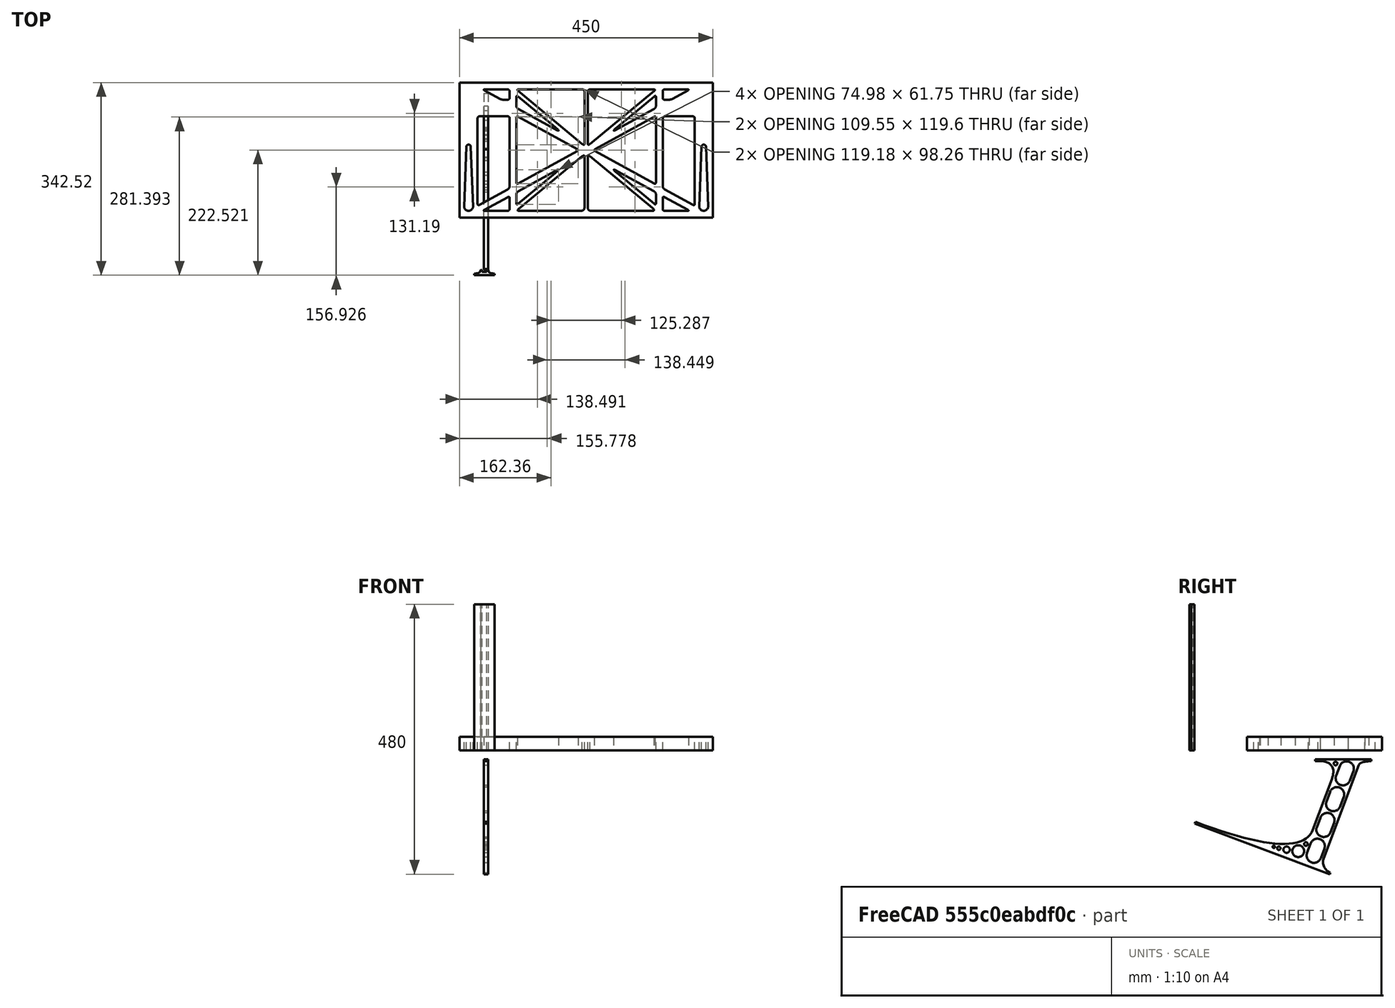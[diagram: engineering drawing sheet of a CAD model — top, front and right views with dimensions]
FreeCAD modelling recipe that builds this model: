
FCSTD DOCUMENT  (FreeCAD 0.19R0.19.2)
Label: laptopStand157FCStd
License: All rights reserved
LicenseURL: http://en.wikipedia.org/wiki/All_rights_reserved
objects: Sketcher::SketchObject×4, Part::Extrusion×3
note: 7 computed .brp shape members not serialized (recipe doc carries the construction recipe); baked Part::Feature solids carry a one-line shape summary decoded from their .brp

FEATURE [Sketcher::SketchObject] Sketch
  FullyConstrained = false
  sketch-geometry (349):
    g0: LineSegment StartX=-10.9272 StartY=-82.7794 StartZ=0 EndX=46.0728 EndY=-51.4823 EndZ=0
    g1: LineSegment StartX=-10.9272 StartY=76.4095 StartZ=0 EndX=-10.9272 EndY=-82.7794 EndZ=0
    g2: LineSegment StartX=46.0728 StartY=76.4095 StartZ=0 EndX=46.0728 EndY=-51.4823 EndZ=0
    g3: LineSegment StartX=-42.9272 StartY=136.221 StartZ=0 EndX=-42.9272 EndY=-103.779 EndZ=0
    g4: LineSegment StartX=407.073 StartY=136.221 StartZ=0 EndX=407.073 EndY=-103.779 EndZ=0
    g5: ArcOfCircle CenterX=-26.9272 CenterY=-83.7794 CenterZ=0 NormalX=0 NormalY=0 NormalZ=1 AngleXU=0 Radius=8 StartAngle=3.14159 EndAngle=6.28319
    g6: ArcOfCircle CenterX=391.073 CenterY=22.1087 CenterZ=0 NormalX=0 NormalY=0 NormalZ=1 AngleXU=0 Radius=8 StartAngle=-4.4e-15 EndAngle=3.14159
    g7: LineSegment StartX=399.073 StartY=22.1087 StartZ=0 EndX=399.073 EndY=-83.7794 EndZ=0
    g8: LineSegment StartX=383.073 StartY=22.1087 StartZ=0 EndX=383.073 EndY=-83.7794 EndZ=0
    g9: ArcOfCircle CenterX=391.073 CenterY=-83.7794 CenterZ=0 NormalX=0 NormalY=0 NormalZ=1 AngleXU=0 Radius=8 StartAngle=3.14159 EndAngle=6.28319
    g10: Circle CenterX=175.022 CenterY=27.0628 CenterZ=0 NormalX=0 NormalY=0 NormalZ=1 AngleXU=0 Radius=1
    g11: Circle CenterX=179.022 CenterY=24.8665 CenterZ=0 NormalX=0 NormalY=0 NormalZ=1 AngleXU=0 Radius=1
    g12: Circle CenterX=179.022 CenterY=27.0628 CenterZ=0 NormalX=0 NormalY=0 NormalZ=1 AngleXU=0 Radius=1
    g13: BSplineCurve PolesCount=3 KnotsCount=2 Degree=2 IsPeriodic=0
    g14: GeomPoint X=175.022 Y=27.0628 Z=0
    g15: GeomPoint X=179.022 Y=27.0628 Z=0
    g16: Circle CenterX=189.124 CenterY=27.0628 CenterZ=0 NormalX=0 NormalY=0 NormalZ=1 AngleXU=0 Radius=1
    g17: Circle CenterX=185.124 CenterY=24.8665 CenterZ=0 NormalX=0 NormalY=0 NormalZ=1 AngleXU=0 Radius=1
    g18: Circle CenterX=185.124 CenterY=27.0628 CenterZ=0 NormalX=0 NormalY=0 NormalZ=1 AngleXU=0 Radius=1
    g19: BSplineCurve PolesCount=3 KnotsCount=2 Degree=2 IsPeriodic=0
    g20: GeomPoint X=189.124 Y=27.0628 Z=0
    g21: GeomPoint X=185.124 Y=27.0628 Z=0
    g22: Circle CenterX=175.022 CenterY=5.37834 CenterZ=0 NormalX=0 NormalY=0 NormalZ=1 AngleXU=0 Radius=1
    g23: Circle CenterX=179.022 CenterY=7.57463 CenterZ=0 NormalX=0 NormalY=0 NormalZ=1 AngleXU=0 Radius=1
    g24: Circle CenterX=179.022 CenterY=5.34704 CenterZ=0 NormalX=0 NormalY=0 NormalZ=1 AngleXU=0 Radius=1
    g25: BSplineCurve PolesCount=3 KnotsCount=2 Degree=2 IsPeriodic=0
    g26: GeomPoint X=175.022 Y=5.37834 Z=0
    g27: GeomPoint X=179.022 Y=5.34704 Z=0
    g28: Circle CenterX=189.124 CenterY=5.37834 CenterZ=0 NormalX=0 NormalY=0 NormalZ=1 AngleXU=0 Radius=1
    g29: Circle CenterX=185.124 CenterY=7.57463 CenterZ=0 NormalX=0 NormalY=0 NormalZ=1 AngleXU=0 Radius=1
    g30: Circle CenterX=185.124 CenterY=5.34704 CenterZ=0 NormalX=0 NormalY=0 NormalZ=1 AngleXU=0 Radius=1
    g31: BSplineCurve PolesCount=3 KnotsCount=2 Degree=2 IsPeriodic=0
    g32: GeomPoint X=189.124 Y=5.37834 Z=0
    g33: GeomPoint X=185.124 Y=5.34704 Z=0
    g34: Circle CenterX=165.871 CenterY=18.1458 CenterZ=0 NormalX=0 NormalY=0 NormalZ=1 AngleXU=0 Radius=1
    g35: Circle CenterX=169.377 CenterY=16.2206 CenterZ=0 NormalX=0 NormalY=0 NormalZ=1 AngleXU=0 Radius=1
    g36: Circle CenterX=165.871 CenterY=14.2954 CenterZ=0 NormalX=0 NormalY=0 NormalZ=1 AngleXU=0 Radius=1
    g37: BSplineCurve PolesCount=3 KnotsCount=2 Degree=2 IsPeriodic=0
    g38: GeomPoint X=165.871 Y=18.1458 Z=0
    g39: GeomPoint X=165.871 Y=14.2954 Z=0
    g40: Circle CenterX=198.275 CenterY=18.1458 CenterZ=0 NormalX=0 NormalY=0 NormalZ=1 AngleXU=0 Radius=1
    g41: Circle CenterX=194.768 CenterY=16.2206 CenterZ=0 NormalX=0 NormalY=0 NormalZ=1 AngleXU=0 Radius=1
    g42: Circle CenterX=198.275 CenterY=14.2954 CenterZ=0 NormalX=0 NormalY=0 NormalZ=1 AngleXU=0 Radius=1
    g43: BSplineCurve PolesCount=3 KnotsCount=2 Degree=2 IsPeriodic=0
    g44: GeomPoint X=198.275 Y=18.1458 Z=0
    g45: GeomPoint X=198.275 Y=14.2954 Z=0
    g46: LineSegment StartX=407.073 StartY=-103.779 StartZ=0 EndX=-42.9272 EndY=-103.779 EndZ=0
    g47: LineSegment StartX=407.073 StartY=136.221 StartZ=0 EndX=-42.9272 EndY=136.221 EndZ=0
    g48: LineSegment StartX=46.0728 StartY=76.4095 StartZ=0 EndX=-10.9272 EndY=76.4095 EndZ=0
    g49: Circle CenterX=125.607 CenterY=54.1951 CenterZ=0 NormalX=0 NormalY=0 NormalZ=1 AngleXU=0 Radius=1
    g50: Circle CenterX=139.632 CenterY=46.4944 CenterZ=0 NormalX=0 NormalY=0 NormalZ=1 AngleXU=0 Radius=1
    g51: Circle CenterX=127.326 CenterY=56.7187 CenterZ=0 NormalX=0 NormalY=0 NormalZ=1 AngleXU=0 Radius=1
    g52: BSplineCurve PolesCount=3 KnotsCount=2 Degree=2 IsPeriodic=0
    g53: GeomPoint X=125.607 Y=54.1951 Z=0
    g54: GeomPoint X=127.326 Y=56.7187 Z=0
    g55: Circle CenterX=236.821 CenterY=56.7187 CenterZ=0 NormalX=0 NormalY=0 NormalZ=1 AngleXU=0 Radius=1
    g56: Circle CenterX=224.513 CenterY=46.4944 CenterZ=0 NormalX=0 NormalY=0 NormalZ=1 AngleXU=0 Radius=1
    g57: Circle CenterX=238.538 CenterY=54.1951 CenterZ=0 NormalX=0 NormalY=0 NormalZ=1 AngleXU=0 Radius=1
    g58: BSplineCurve PolesCount=3 KnotsCount=2 Degree=2 IsPeriodic=0
    g59: GeomPoint X=236.821 Y=56.7187 Z=0
    g60: GeomPoint X=238.538 Y=54.1951 Z=0
    g61: Circle CenterX=238.538 CenterY=-21.7539 CenterZ=0 NormalX=0 NormalY=0 NormalZ=1 AngleXU=0 Radius=1
    g62: Circle CenterX=224.513 CenterY=-14.0532 CenterZ=0 NormalX=0 NormalY=0 NormalZ=1 AngleXU=0 Radius=1
    g63: Circle CenterX=236.821 CenterY=-24.2775 CenterZ=0 NormalX=0 NormalY=0 NormalZ=1 AngleXU=0 Radius=1
    g64: BSplineCurve PolesCount=3 KnotsCount=2 Degree=2 IsPeriodic=0
    g65: GeomPoint X=238.538 Y=-21.7539 Z=0
    g66: GeomPoint X=236.821 Y=-24.2775 Z=0
    g67: Circle CenterX=125.607 CenterY=-21.7539 CenterZ=0 NormalX=0 NormalY=0 NormalZ=1 AngleXU=0 Radius=1
    g68: Circle CenterX=139.632 CenterY=-14.0532 CenterZ=0 NormalX=0 NormalY=0 NormalZ=1 AngleXU=0 Radius=1
    g69: Circle CenterX=127.325 CenterY=-24.2775 CenterZ=0 NormalX=0 NormalY=0 NormalZ=1 AngleXU=0 Radius=1
    g70: BSplineCurve PolesCount=3 KnotsCount=2 Degree=2 IsPeriodic=0
    g71: GeomPoint X=125.607 Y=-21.7539 Z=0
    g72: GeomPoint X=127.325 Y=-24.2775 Z=0
    g73: Circle CenterX=302.996 CenterY=111.695 CenterZ=0 NormalX=0 NormalY=0 NormalZ=1 AngleXU=0 Radius=1
    g74: Circle CenterX=306.073 CenterY=114.251 CenterZ=0 NormalX=0 NormalY=0 NormalZ=1 AngleXU=0 Radius=1
    g75: Circle CenterX=306.073 CenterY=110.251 CenterZ=0 NormalX=0 NormalY=0 NormalZ=1 AngleXU=0 Radius=1
    g76: BSplineCurve PolesCount=3 KnotsCount=2 Degree=2 IsPeriodic=0
    g77: GeomPoint X=302.996 Y=111.695 Z=0
    g78: GeomPoint X=306.073 Y=110.251 Z=0
    g79: Circle CenterX=306.073 CenterY=95.2763 CenterZ=0 NormalX=0 NormalY=0 NormalZ=1 AngleXU=0 Radius=1
    g80: Circle CenterX=306.073 CenterY=91.2763 CenterZ=0 NormalX=0 NormalY=0 NormalZ=1 AngleXU=0 Radius=1
    g81: Circle CenterX=302.567 CenterY=89.3511 CenterZ=0 NormalX=0 NormalY=0 NormalZ=1 AngleXU=0 Radius=1
    g82: BSplineCurve PolesCount=3 KnotsCount=2 Degree=2 IsPeriodic=0
    g83: GeomPoint X=306.073 Y=95.2763 Z=0
    g84: GeomPoint X=302.567 Y=89.3511 Z=0
    g85: LineSegment StartX=306.073 StartY=110.251 StartZ=0 EndX=306.073 EndY=95.2763 EndZ=0
    g86: LineSegment StartX=302.996 StartY=111.695 StartZ=0 EndX=236.821 EndY=56.7187 EndZ=0
    g87: LineSegment StartX=238.538 StartY=54.1951 StartZ=0 EndX=302.567 EndY=89.3511 EndZ=0
    g88: Circle CenterX=61.1496 CenterY=111.695 CenterZ=0 NormalX=0 NormalY=0 NormalZ=1 AngleXU=0 Radius=1
    g89: Circle CenterX=58.0728 CenterY=114.251 CenterZ=0 NormalX=0 NormalY=0 NormalZ=1 AngleXU=0 Radius=1
    g90: Circle CenterX=58.0728 CenterY=110.251 CenterZ=0 NormalX=0 NormalY=0 NormalZ=1 AngleXU=0 Radius=1
    g91: BSplineCurve PolesCount=3 KnotsCount=2 Degree=2 IsPeriodic=0
    g92: GeomPoint X=61.1496 Y=111.695 Z=0
    g93: GeomPoint X=58.0728 Y=110.251 Z=0
    g94: Circle CenterX=61.5791 CenterY=89.3511 CenterZ=0 NormalX=0 NormalY=0 NormalZ=1 AngleXU=0 Radius=1
    g95: Circle CenterX=58.0728 CenterY=91.2763 CenterZ=0 NormalX=0 NormalY=0 NormalZ=1 AngleXU=0 Radius=1
    g96: Circle CenterX=58.0728 CenterY=95.2763 CenterZ=0 NormalX=0 NormalY=0 NormalZ=1 AngleXU=0 Radius=1
    g97: BSplineCurve PolesCount=3 KnotsCount=2 Degree=2 IsPeriodic=0
    g98: GeomPoint X=61.5791 Y=89.3511 Z=0
    g99: GeomPoint X=58.0728 Y=95.2763 Z=0
    g100: LineSegment StartX=58.0728 StartY=110.251 StartZ=0 EndX=58.0728 EndY=95.2763 EndZ=0
    g101: LineSegment StartX=61.1496 StartY=111.695 StartZ=0 EndX=127.326 EndY=56.7187 EndZ=0
    g102: LineSegment StartX=125.607 StartY=54.1951 StartZ=0 EndX=61.5791 EndY=89.3511 EndZ=0
    g103: Circle CenterX=61.5791 CenterY=-56.9099 CenterZ=0 NormalX=0 NormalY=0 NormalZ=1 AngleXU=0 Radius=1
    g104: Circle CenterX=58.0728 CenterY=-58.8351 CenterZ=0 NormalX=0 NormalY=0 NormalZ=1 AngleXU=0 Radius=1
    g105: Circle CenterX=58.0728 CenterY=-62.8351 CenterZ=0 NormalX=0 NormalY=0 NormalZ=1 AngleXU=0 Radius=1
    g106: BSplineCurve PolesCount=3 KnotsCount=2 Degree=2 IsPeriodic=0
    g107: GeomPoint X=61.5791 Y=-56.9099 Z=0
    g108: GeomPoint X=58.0728 Y=-62.8351 Z=0
    g109: Circle CenterX=58.0728 CenterY=-77.8102 CenterZ=0 NormalX=0 NormalY=0 NormalZ=1 AngleXU=0 Radius=1
    g110: Circle CenterX=58.0728 CenterY=-81.8102 CenterZ=0 NormalX=0 NormalY=0 NormalZ=1 AngleXU=0 Radius=1
    g111: Circle CenterX=61.1496 CenterY=-79.2541 CenterZ=0 NormalX=0 NormalY=0 NormalZ=1 AngleXU=0 Radius=1
    g112: BSplineCurve PolesCount=3 KnotsCount=2 Degree=2 IsPeriodic=0
    g113: GeomPoint X=58.0728 Y=-77.8102 Z=0
    g114: GeomPoint X=61.1496 Y=-79.2541 Z=0
    g115: LineSegment StartX=58.0728 StartY=-62.8351 StartZ=0 EndX=58.0728 EndY=-77.8102 EndZ=0
    g116: LineSegment StartX=61.1496 StartY=-79.2541 StartZ=0 EndX=127.325 EndY=-24.2775 EndZ=0
    g117: LineSegment StartX=125.607 StartY=-21.7539 StartZ=0 EndX=61.5791 EndY=-56.9099 EndZ=0
    g118: Circle CenterX=302.567 CenterY=-56.9099 CenterZ=0 NormalX=0 NormalY=0 NormalZ=1 AngleXU=0 Radius=1
    g119: Circle CenterX=306.073 CenterY=-58.8351 CenterZ=0 NormalX=0 NormalY=0 NormalZ=1 AngleXU=0 Radius=1
    g120: Circle CenterX=306.073 CenterY=-62.8351 CenterZ=0 NormalX=0 NormalY=0 NormalZ=1 AngleXU=0 Radius=1
    g121: BSplineCurve PolesCount=3 KnotsCount=2 Degree=2 IsPeriodic=0
    g122: GeomPoint X=302.567 Y=-56.9099 Z=0
    g123: GeomPoint X=306.073 Y=-62.8351 Z=0
    g124: Circle CenterX=302.996 CenterY=-79.2541 CenterZ=0 NormalX=0 NormalY=0 NormalZ=1 AngleXU=0 Radius=1
    g125: Circle CenterX=306.073 CenterY=-81.8102 CenterZ=0 NormalX=0 NormalY=0 NormalZ=1 AngleXU=0 Radius=1
    g126: Circle CenterX=306.073 CenterY=-77.8102 CenterZ=0 NormalX=0 NormalY=0 NormalZ=1 AngleXU=0 Radius=1
    g127: BSplineCurve PolesCount=3 KnotsCount=2 Degree=2 IsPeriodic=0
    g128: GeomPoint X=302.996 Y=-79.2541 Z=0
    g129: GeomPoint X=306.073 Y=-77.8102 Z=0
    g130: LineSegment StartX=306.073 StartY=-62.8351 StartZ=0 EndX=306.073 EndY=-77.8102 EndZ=0
    g131: LineSegment StartX=302.996 StartY=-79.2541 StartZ=0 EndX=236.821 EndY=-24.2775 EndZ=0
    g132: LineSegment StartX=238.538 StartY=-21.7539 StartZ=0 EndX=302.567 EndY=-56.9099 EndZ=0
    g133: Circle CenterX=61.6457 CenterY=-88.8112 CenterZ=0 NormalX=0 NormalY=0 NormalZ=1 AngleXU=0 Radius=1
    g134: Circle CenterX=58.0728 CenterY=-91.7794 CenterZ=0 NormalX=0 NormalY=0 NormalZ=1 AngleXU=0 Radius=1
    g135: Circle CenterX=63.9135 CenterY=-91.7794 CenterZ=0 NormalX=0 NormalY=0 NormalZ=1 AngleXU=0 Radius=1
    g136: BSplineCurve PolesCount=3 KnotsCount=2 Degree=2 IsPeriodic=0
    g137: GeomPoint X=61.6457 Y=-88.8112 Z=0
    g138: GeomPoint X=63.9135 Y=-91.7794 Z=0
    g139: Circle CenterX=179.022 CenterY=-85.8163 CenterZ=0 NormalX=0 NormalY=0 NormalZ=1 AngleXU=0 Radius=1
    g140: Circle CenterX=179.022 CenterY=-91.7794 CenterZ=0 NormalX=0 NormalY=0 NormalZ=1 AngleXU=0 Radius=1
    g141: Circle CenterX=171.895 CenterY=-91.7794 CenterZ=0 NormalX=0 NormalY=0 NormalZ=1 AngleXU=0 Radius=1
    g142: BSplineCurve PolesCount=3 KnotsCount=2 Degree=2 IsPeriodic=0
    g143: GeomPoint X=179.022 Y=-85.8163 Z=0
    g144: GeomPoint X=171.895 Y=-91.7794 Z=0
    g145: Circle CenterX=185.124 CenterY=-86.2028 CenterZ=0 NormalX=0 NormalY=0 NormalZ=1 AngleXU=0 Radius=1
    g146: Circle CenterX=185.124 CenterY=-91.7794 CenterZ=0 NormalX=0 NormalY=0 NormalZ=1 AngleXU=0 Radius=1
    g147: Circle CenterX=191.747 CenterY=-91.7794 CenterZ=0 NormalX=0 NormalY=0 NormalZ=1 AngleXU=0 Radius=1
    g148: BSplineCurve PolesCount=3 KnotsCount=2 Degree=2 IsPeriodic=0
    g149: GeomPoint X=185.124 Y=-86.2028 Z=0
    g150: GeomPoint X=191.747 Y=-91.7794 Z=0
    g151: Circle CenterX=299.888 CenterY=-86.6413 CenterZ=0 NormalX=0 NormalY=0 NormalZ=1 AngleXU=0 Radius=1
    g152: Circle CenterX=306.073 CenterY=-91.7794 CenterZ=0 NormalX=0 NormalY=0 NormalZ=1 AngleXU=0 Radius=1
    g153: Circle CenterX=298.776 CenterY=-91.7794 CenterZ=0 NormalX=0 NormalY=0 NormalZ=1 AngleXU=0 Radius=1
    g154: BSplineCurve PolesCount=3 KnotsCount=2 Degree=2 IsPeriodic=0
    g155: GeomPoint X=299.888 Y=-86.6413 Z=0
    g156: GeomPoint X=298.776 Y=-91.7794 Z=0
    g157: LineSegment StartX=189.124 StartY=5.37834 StartZ=0 EndX=299.888 EndY=-86.6413 EndZ=0
    g158: LineSegment StartX=298.776 StartY=-91.7794 StartZ=0 EndX=191.747 EndY=-91.7794 EndZ=0
    g159: LineSegment StartX=185.124 StartY=-86.2028 StartZ=0 EndX=185.124 EndY=5.34704 EndZ=0
    g160: LineSegment StartX=179.022 StartY=5.34704 StartZ=0 EndX=179.022 EndY=-85.8163 EndZ=0
    g161: LineSegment StartX=171.895 StartY=-91.7794 StartZ=0 EndX=63.9135 EndY=-91.7794 EndZ=0
    g162: LineSegment StartX=61.6457 StartY=-88.8112 StartZ=0 EndX=175.022 EndY=5.37834 EndZ=0
    g163: Circle CenterX=302.073 CenterY=124.221 CenterZ=0 NormalX=0 NormalY=0 NormalZ=1 AngleXU=0 Radius=1
    g164: Circle CenterX=306.073 CenterY=124.221 CenterZ=0 NormalX=0 NormalY=0 NormalZ=1 AngleXU=0 Radius=1
    g165: Circle CenterX=302.996 CenterY=121.665 CenterZ=0 NormalX=0 NormalY=0 NormalZ=1 AngleXU=0 Radius=1
    g166: BSplineCurve PolesCount=3 KnotsCount=2 Degree=2 IsPeriodic=0
    g167: GeomPoint X=302.073 Y=124.221 Z=0
    g168: GeomPoint X=302.996 Y=121.665 Z=0
    g169: Circle CenterX=189.124 CenterY=124.221 CenterZ=0 NormalX=0 NormalY=0 NormalZ=1 AngleXU=0 Radius=1
    g170: Circle CenterX=185.124 CenterY=124.221 CenterZ=0 NormalX=0 NormalY=0 NormalZ=1 AngleXU=0 Radius=1
    g171: Circle CenterX=185.124 CenterY=120.221 CenterZ=0 NormalX=0 NormalY=0 NormalZ=1 AngleXU=0 Radius=1
    g172: BSplineCurve PolesCount=3 KnotsCount=2 Degree=2 IsPeriodic=0
    g173: GeomPoint X=189.124 Y=124.221 Z=0
    g174: GeomPoint X=185.124 Y=120.221 Z=0
    g175: Circle CenterX=175.022 CenterY=124.221 CenterZ=0 NormalX=0 NormalY=0 NormalZ=1 AngleXU=0 Radius=1
    g176: Circle CenterX=179.022 CenterY=124.221 CenterZ=0 NormalX=0 NormalY=0 NormalZ=1 AngleXU=0 Radius=1
    g177: Circle CenterX=179.022 CenterY=120.221 CenterZ=0 NormalX=0 NormalY=0 NormalZ=1 AngleXU=0 Radius=1
    g178: BSplineCurve PolesCount=3 KnotsCount=2 Degree=2 IsPeriodic=0
    g179: GeomPoint X=175.022 Y=124.221 Z=0
    g180: GeomPoint X=179.022 Y=120.221 Z=0
    g181: Circle CenterX=62.0728 CenterY=124.221 CenterZ=0 NormalX=0 NormalY=0 NormalZ=1 AngleXU=0 Radius=1
    g182: Circle CenterX=58.0728 CenterY=124.221 CenterZ=0 NormalX=0 NormalY=0 NormalZ=1 AngleXU=0 Radius=1
    g183: Circle CenterX=61.1496 CenterY=121.665 CenterZ=0 NormalX=0 NormalY=0 NormalZ=1 AngleXU=0 Radius=1
    g184: BSplineCurve PolesCount=3 KnotsCount=2 Degree=2 IsPeriodic=0
    g185: GeomPoint X=62.0728 Y=124.221 Z=0
    g186: GeomPoint X=61.1496 Y=121.665 Z=0
    g187: LineSegment StartX=62.0728 StartY=124.221 StartZ=0 EndX=175.022 EndY=124.221 EndZ=0
    g188: LineSegment StartX=179.022 StartY=120.221 StartZ=0 EndX=179.022 EndY=27.0628 EndZ=0
    g189: LineSegment StartX=185.124 StartY=27.0628 StartZ=0 EndX=185.124 EndY=120.221 EndZ=0
    g190: LineSegment StartX=189.124 StartY=124.221 StartZ=0 EndX=302.073 EndY=124.221 EndZ=0
    g191: LineSegment StartX=302.996 StartY=121.665 StartZ=0 EndX=189.124 EndY=27.0628 EndZ=0
    g192: LineSegment StartX=175.022 StartY=27.0628 StartZ=0 EndX=61.1496 EndY=121.665 EndZ=0
    g193: Circle CenterX=61.5791 CenterY=75.4095 CenterZ=0 NormalX=0 NormalY=0 NormalZ=1 AngleXU=0 Radius=1
    g194: Circle CenterX=58.0728 CenterY=77.3346 CenterZ=0 NormalX=0 NormalY=0 NormalZ=1 AngleXU=0 Radius=1
    g195: Circle CenterX=58.0728 CenterY=73.3346 CenterZ=0 NormalX=0 NormalY=0 NormalZ=1 AngleXU=0 Radius=1
    g196: BSplineCurve PolesCount=3 KnotsCount=2 Degree=2 IsPeriodic=0
    g197: GeomPoint X=61.5791 Y=75.4095 Z=0
    g198: GeomPoint X=58.0728 Y=73.3346 Z=0
    g199: Circle CenterX=58.0728 CenterY=-40.8935 CenterZ=0 NormalX=0 NormalY=0 NormalZ=1 AngleXU=0 Radius=1
    g200: Circle CenterX=58.0728 CenterY=-44.8935 CenterZ=0 NormalX=0 NormalY=0 NormalZ=1 AngleXU=0 Radius=1
    g201: Circle CenterX=61.5791 CenterY=-42.9683 CenterZ=0 NormalX=0 NormalY=0 NormalZ=1 AngleXU=0 Radius=1
    g202: BSplineCurve PolesCount=3 KnotsCount=2 Degree=2 IsPeriodic=0
    g203: GeomPoint X=58.0728 Y=-40.8935 Z=0
    g204: GeomPoint X=61.5791 Y=-42.9683 Z=0
    g205: LineSegment StartX=61.5791 StartY=-42.9683 StartZ=0 EndX=165.871 EndY=14.2954 EndZ=0
    g206: LineSegment StartX=165.871 StartY=18.1458 StartZ=0 EndX=61.5791 EndY=75.4095 EndZ=0
    g207: LineSegment StartX=58.0728 StartY=73.3346 StartZ=0 EndX=58.0728 EndY=-40.8935 EndZ=0
    g208: Circle CenterX=302.567 CenterY=-42.9683 CenterZ=0 NormalX=0 NormalY=0 NormalZ=1 AngleXU=0 Radius=1
    g209: Circle CenterX=306.073 CenterY=-44.8935 CenterZ=0 NormalX=0 NormalY=0 NormalZ=1 AngleXU=0 Radius=1
    g210: Circle CenterX=306.073 CenterY=-40.8935 CenterZ=0 NormalX=0 NormalY=0 NormalZ=1 AngleXU=0 Radius=1
    g211: BSplineCurve PolesCount=3 KnotsCount=2 Degree=2 IsPeriodic=0
    g212: GeomPoint X=302.567 Y=-42.9683 Z=0
    g213: GeomPoint X=306.073 Y=-40.8935 Z=0
    g214: Circle CenterX=306.073 CenterY=73.3346 CenterZ=0 NormalX=0 NormalY=0 NormalZ=1 AngleXU=0 Radius=1
    g215: Circle CenterX=306.073 CenterY=77.3346 CenterZ=0 NormalX=0 NormalY=0 NormalZ=1 AngleXU=0 Radius=1
    g216: Circle CenterX=302.567 CenterY=75.4095 CenterZ=0 NormalX=0 NormalY=0 NormalZ=1 AngleXU=0 Radius=1
    g217: BSplineCurve PolesCount=3 KnotsCount=2 Degree=2 IsPeriodic=0
    g218: GeomPoint X=306.073 Y=73.3346 Z=0
    g219: GeomPoint X=302.567 Y=75.4095 Z=0
    g220: LineSegment StartX=302.567 StartY=-42.9683 StartZ=0 EndX=198.275 EndY=14.2954 EndZ=0
    g221: LineSegment StartX=198.275 StartY=18.1458 StartZ=0 EndX=302.567 EndY=75.4095 EndZ=0
    g222: LineSegment StartX=306.073 StartY=73.3346 StartZ=0 EndX=306.073 EndY=-40.8935 EndZ=0
    g223: LineSegment StartX=322.073 StartY=105.865 StartZ=0 EndX=328.643 EndY=105.865 EndZ=0
    g224: LineSegment StartX=318.073 StartY=120.221 StartZ=0 EndX=318.073 EndY=109.865 EndZ=0
    g225: LineSegment StartX=336.157 StartY=107.779 StartZ=0 EndX=362.567 EndY=122.294 EndZ=0
    g226: Circle CenterX=362.073 CenterY=124.221 CenterZ=0 NormalX=0 NormalY=0 NormalZ=1 AngleXU=0 Radius=1
    g227: Circle CenterX=366.073 CenterY=124.221 CenterZ=0 NormalX=0 NormalY=0 NormalZ=1 AngleXU=0 Radius=1
    g228: Circle CenterX=362.567 CenterY=122.294 CenterZ=0 NormalX=0 NormalY=0 NormalZ=1 AngleXU=0 Radius=1
    g229: BSplineCurve PolesCount=3 KnotsCount=2 Degree=2 IsPeriodic=0
    g230: GeomPoint X=362.073 Y=124.221 Z=0
    g231: GeomPoint X=362.567 Y=122.294 Z=0
    g232: Circle CenterX=322.073 CenterY=124.221 CenterZ=0 NormalX=0 NormalY=0 NormalZ=1 AngleXU=0 Radius=1
    g233: Circle CenterX=318.073 CenterY=124.221 CenterZ=0 NormalX=0 NormalY=0 NormalZ=1 AngleXU=0 Radius=1
    g234: Circle CenterX=318.073 CenterY=120.221 CenterZ=0 NormalX=0 NormalY=0 NormalZ=1 AngleXU=0 Radius=1
    g235: BSplineCurve PolesCount=3 KnotsCount=2 Degree=2 IsPeriodic=0
    g236: GeomPoint X=322.073 Y=124.221 Z=0
    g237: GeomPoint X=318.073 Y=120.221 Z=0
    g238: Circle CenterX=322.073 CenterY=105.865 CenterZ=0 NormalX=0 NormalY=0 NormalZ=1 AngleXU=0 Radius=1
    g239: Circle CenterX=318.073 CenterY=105.865 CenterZ=0 NormalX=0 NormalY=0 NormalZ=1 AngleXU=0 Radius=1
    g240: Circle CenterX=318.073 CenterY=109.865 CenterZ=0 NormalX=0 NormalY=0 NormalZ=1 AngleXU=0 Radius=1
    g241: BSplineCurve PolesCount=3 KnotsCount=2 Degree=2 IsPeriodic=0
    g242: GeomPoint X=322.073 Y=105.865 Z=0
    g243: GeomPoint X=318.073 Y=109.865 Z=0
    g244: Circle CenterX=336.157 CenterY=107.779 CenterZ=0 NormalX=0 NormalY=0 NormalZ=1 AngleXU=0 Radius=1
    g245: Circle CenterX=332.651 CenterY=105.853 CenterZ=0 NormalX=0 NormalY=0 NormalZ=1 AngleXU=0 Radius=1
    g246: Circle CenterX=328.643 CenterY=105.865 CenterZ=0 NormalX=0 NormalY=0 NormalZ=1 AngleXU=0 Radius=1
    g247: BSplineCurve PolesCount=3 KnotsCount=2 Degree=2 IsPeriodic=0
    g248: GeomPoint X=336.157 Y=107.779 Z=0
    g249: GeomPoint X=328.643 Y=105.865 Z=0
    g250: LineSegment StartX=322.073 StartY=124.221 StartZ=0 EndX=362.073 EndY=124.221 EndZ=0
    g251: Circle CenterX=371.567 CenterY=-80.8644 CenterZ=0 NormalX=0 NormalY=0 NormalZ=1 AngleXU=0 Radius=1
    g252: Circle CenterX=375.073 CenterY=-82.7896 CenterZ=0 NormalX=0 NormalY=0 NormalZ=1 AngleXU=0 Radius=1
    g253: Circle CenterX=375.073 CenterY=-78.7896 CenterZ=0 NormalX=0 NormalY=0 NormalZ=1 AngleXU=0 Radius=1
    g254: BSplineCurve PolesCount=3 KnotsCount=2 Degree=2 IsPeriodic=0
    g255: GeomPoint X=371.567 Y=-80.8644 Z=0
    g256: GeomPoint X=375.073 Y=-78.7896 Z=0
    g257: Circle CenterX=321.579 CenterY=-53.4075 CenterZ=0 NormalX=0 NormalY=0 NormalZ=1 AngleXU=0 Radius=1
    g258: Circle CenterX=318.073 CenterY=-51.4823 CenterZ=0 NormalX=0 NormalY=0 NormalZ=1 AngleXU=0 Radius=1
    g259: Circle CenterX=318.073 CenterY=-47.4805 CenterZ=0 NormalX=0 NormalY=0 NormalZ=1 AngleXU=0 Radius=1
    g260: BSplineCurve PolesCount=3 KnotsCount=2 Degree=2 IsPeriodic=0
    g261: GeomPoint X=321.579 Y=-53.4075 Z=0
    g262: GeomPoint X=318.073 Y=-47.4805 Z=0
    g263: LineSegment StartX=371.567 StartY=-80.8644 StartZ=0 EndX=321.579 EndY=-53.4075 EndZ=0
    g264: Circle CenterX=321.579 CenterY=-67.3492 CenterZ=0 NormalX=0 NormalY=0 NormalZ=1 AngleXU=0 Radius=1
    g265: Circle CenterX=318.073 CenterY=-65.424 CenterZ=0 NormalX=0 NormalY=0 NormalZ=1 AngleXU=0 Radius=1
    g266: Circle CenterX=318.073 CenterY=-69.424 CenterZ=0 NormalX=0 NormalY=0 NormalZ=1 AngleXU=0 Radius=1
    g267: BSplineCurve PolesCount=3 KnotsCount=2 Degree=2 IsPeriodic=0
    g268: GeomPoint X=321.579 Y=-67.3492 Z=0
    g269: GeomPoint X=318.073 Y=-69.424 Z=0
    g270: Circle CenterX=362.567 CenterY=-89.8542 CenterZ=0 NormalX=0 NormalY=0 NormalZ=1 AngleXU=0 Radius=1
    g271: Circle CenterX=366.073 CenterY=-91.7794 CenterZ=0 NormalX=0 NormalY=0 NormalZ=1 AngleXU=0 Radius=1
    g272: Circle CenterX=362.073 CenterY=-91.7794 CenterZ=0 NormalX=0 NormalY=0 NormalZ=1 AngleXU=0 Radius=1
    g273: BSplineCurve PolesCount=3 KnotsCount=2 Degree=2 IsPeriodic=0
    g274: GeomPoint X=362.567 Y=-89.8542 Z=0
    g275: GeomPoint X=362.073 Y=-91.7794 Z=0
    g276: Circle CenterX=322.073 CenterY=-91.7794 CenterZ=0 NormalX=0 NormalY=0 NormalZ=1 AngleXU=0 Radius=1
    g277: Circle CenterX=318.073 CenterY=-91.7794 CenterZ=0 NormalX=0 NormalY=0 NormalZ=1 AngleXU=0 Radius=1
    g278: Circle CenterX=318.073 CenterY=-87.7794 CenterZ=0 NormalX=0 NormalY=0 NormalZ=1 AngleXU=0 Radius=1
    g279: BSplineCurve PolesCount=3 KnotsCount=2 Degree=2 IsPeriodic=0
    g280: GeomPoint X=322.073 Y=-91.7794 Z=0
    g281: GeomPoint X=318.073 Y=-87.7794 Z=0
    g282: LineSegment StartX=362.567 StartY=-89.8542 StartZ=0 EndX=321.579 EndY=-67.3492 EndZ=0
    g283: LineSegment StartX=318.073 StartY=-69.424 StartZ=0 EndX=318.073 EndY=-87.7794 EndZ=0
    g284: LineSegment StartX=322.073 StartY=-91.7794 StartZ=0 EndX=362.073 EndY=-91.7794 EndZ=0
    g285: Circle CenterX=2.07281 CenterY=124.221 CenterZ=0 NormalX=0 NormalY=0 NormalZ=1 AngleXU=0 Radius=1
    g286: Circle CenterX=1.57905 CenterY=122.295 CenterZ=0 NormalX=0 NormalY=0 NormalZ=1 AngleXU=0 Radius=1
    g287: BSplineCurve PolesCount=3 KnotsCount=2 Degree=2 IsPeriodic=0
    g288: GeomPoint X=2.07281 Y=124.221 Z=0
    g289: GeomPoint X=1.57905 Y=122.295 Z=0
    g290: Circle CenterX=42.0728 CenterY=124.221 CenterZ=0 NormalX=0 NormalY=0 NormalZ=1 AngleXU=0 Radius=1
    g291: Circle CenterX=46.0728 CenterY=124.221 CenterZ=0 NormalX=0 NormalY=0 NormalZ=1 AngleXU=0 Radius=1
    g292: Circle CenterX=46.0728 CenterY=120.221 CenterZ=0 NormalX=0 NormalY=0 NormalZ=1 AngleXU=0 Radius=1
    g293: BSplineCurve PolesCount=3 KnotsCount=2 Degree=2 IsPeriodic=0
    g294: GeomPoint X=42.0728 Y=124.221 Z=0
    g295: GeomPoint X=46.0728 Y=120.221 Z=0
    g296: Circle CenterX=46.0728 CenterY=109.865 CenterZ=0 NormalX=0 NormalY=0 NormalZ=1 AngleXU=0 Radius=1
    g297: Circle CenterX=46.0728 CenterY=105.865 CenterZ=0 NormalX=0 NormalY=0 NormalZ=1 AngleXU=0 Radius=1
    g298: Circle CenterX=42.0728 CenterY=105.865 CenterZ=0 NormalX=0 NormalY=0 NormalZ=1 AngleXU=0 Radius=1
    g299: BSplineCurve PolesCount=3 KnotsCount=2 Degree=2 IsPeriodic=0
    g300: GeomPoint X=46.0728 Y=109.865 Z=0
    g301: GeomPoint X=42.0728 Y=105.865 Z=0
    g302: Circle CenterX=35.5028 CenterY=105.865 CenterZ=0 NormalX=0 NormalY=0 NormalZ=1 AngleXU=0 Radius=1
    g303: Circle CenterX=31.5028 CenterY=105.865 CenterZ=0 NormalX=0 NormalY=0 NormalZ=1 AngleXU=0 Radius=1
    g304: Circle CenterX=27.9965 CenterY=107.79 CenterZ=0 NormalX=0 NormalY=0 NormalZ=1 AngleXU=0 Radius=1
    g305: BSplineCurve PolesCount=3 KnotsCount=2 Degree=2 IsPeriodic=0
    g306: GeomPoint X=35.5028 Y=105.865 Z=0
    g307: GeomPoint X=27.9965 Y=107.79 Z=0
    g308: LineSegment StartX=2.07281 StartY=124.221 StartZ=0 EndX=42.0728 EndY=124.221 EndZ=0
    g309: LineSegment StartX=46.0728 StartY=120.221 StartZ=0 EndX=46.0728 EndY=109.865 EndZ=0
    g310: LineSegment StartX=42.0728 StartY=105.865 StartZ=0 EndX=35.5028 EndY=105.865 EndZ=0
    g311: LineSegment StartX=27.9965 StartY=107.79 StartZ=0 EndX=1.57905 EndY=122.295 EndZ=0
    g312: Circle CenterX=42.5666 CenterY=-67.3492 CenterZ=0 NormalX=0 NormalY=0 NormalZ=1 AngleXU=0 Radius=1
    g313: Circle CenterX=46.0728 CenterY=-65.424 CenterZ=0 NormalX=0 NormalY=0 NormalZ=1 AngleXU=0 Radius=1
    g314: Circle CenterX=46.0728 CenterY=-69.424 CenterZ=0 NormalX=0 NormalY=0 NormalZ=1 AngleXU=0 Radius=1
    g315: BSplineCurve PolesCount=3 KnotsCount=2 Degree=2 IsPeriodic=0
    g316: GeomPoint X=42.5666 Y=-67.3492 Z=0
    g317: GeomPoint X=46.0728 Y=-69.424 Z=0
    g318: Circle CenterX=46.0728 CenterY=-87.7794 CenterZ=0 NormalX=0 NormalY=0 NormalZ=1 AngleXU=0 Radius=1
    g319: Circle CenterX=46.0728 CenterY=-91.7794 CenterZ=0 NormalX=0 NormalY=0 NormalZ=1 AngleXU=0 Radius=1
    g320: Circle CenterX=42.0728 CenterY=-91.7794 CenterZ=0 NormalX=0 NormalY=0 NormalZ=1 AngleXU=0 Radius=1
    g321: BSplineCurve PolesCount=3 KnotsCount=2 Degree=2 IsPeriodic=0
    g322: GeomPoint X=46.0728 Y=-87.7794 Z=0
    g323: GeomPoint X=42.0728 Y=-91.7794 Z=0
    g324: Circle CenterX=2.07281 CenterY=-91.7794 CenterZ=0 NormalX=0 NormalY=0 NormalZ=1 AngleXU=0 Radius=1
    g325: Circle CenterX=-1.92719 CenterY=-91.7794 CenterZ=0 NormalX=0 NormalY=0 NormalZ=1 AngleXU=0 Radius=1
    g326: Circle CenterX=1.57905 CenterY=-89.8542 CenterZ=0 NormalX=0 NormalY=0 NormalZ=1 AngleXU=0 Radius=1
    g327: BSplineCurve PolesCount=3 KnotsCount=2 Degree=2 IsPeriodic=0
    g328: GeomPoint X=2.07281 Y=-91.7794 Z=0
    g329: GeomPoint X=1.57905 Y=-89.8542 Z=0
    g330: LineSegment StartX=2.07281 StartY=-91.7794 StartZ=0 EndX=42.0728 EndY=-91.7794 EndZ=0
    g331: LineSegment StartX=46.0728 StartY=-87.7794 StartZ=0 EndX=46.0728 EndY=-69.424 EndZ=0
    g332: LineSegment StartX=42.5666 StartY=-67.3492 StartZ=0 EndX=1.57905 EndY=-89.8542 EndZ=0
    g333: Circle CenterX=322.073 CenterY=76.4095 CenterZ=0 NormalX=0 NormalY=0 NormalZ=1 AngleXU=0 Radius=4
    g334: BSplineCurve PolesCount=3 KnotsCount=2 Degree=2 IsPeriodic=0
    g335: GeomPoint X=318.073 Y=72.4095 Z=0
    g336: GeomPoint X=322.073 Y=76.4095 Z=0
    g337: Circle CenterX=375.073 CenterY=72.4095 CenterZ=0 NormalX=0 NormalY=0 NormalZ=1 AngleXU=0 Radius=1
    g338: Circle CenterX=375.073 CenterY=76.4095 CenterZ=0 NormalX=0 NormalY=0 NormalZ=1 AngleXU=0 Radius=1
    g339: Circle CenterX=371.073 CenterY=76.4095 CenterZ=0 NormalX=0 NormalY=0 NormalZ=1 AngleXU=0 Radius=1
    g340: BSplineCurve PolesCount=3 KnotsCount=2 Degree=2 IsPeriodic=0
    g341: GeomPoint X=375.073 Y=72.4095 Z=0
    g342: GeomPoint X=371.073 Y=76.4095 Z=0
    g343: LineSegment StartX=322.073 StartY=76.4095 StartZ=0 EndX=371.073 EndY=76.4095 EndZ=0
    g344: LineSegment StartX=318.073 StartY=72.4095 StartZ=0 EndX=318.073 EndY=-47.4805 EndZ=0
    g345: LineSegment StartX=375.073 StartY=72.4095 StartZ=0 EndX=375.073 EndY=-78.7896 EndZ=0
    g346: ArcOfCircle CenterX=-26.9272 CenterY=22.1087 CenterZ=0 NormalX=0 NormalY=0 NormalZ=1 AngleXU=0 Radius=4 StartAngle=5e-16 EndAngle=3.14159
    g347: LineSegment StartX=-30.9272 StartY=22.1087 StartZ=0 EndX=-34.9272 EndY=-83.7794 EndZ=0
    g348: LineSegment StartX=-18.9272 StartY=-83.7794 StartZ=0 EndX=-22.9272 EndY=22.1087 EndZ=0
  constraints (572):
    c: Coincident(g0,g2)
    c: Block(g0)
    c: Block(g1)
    c: Vertical(g3)
    c: Vertical(g4)
    c: Block(g4)
    c: Block(g3)
    c: Tangent(g6,g7) = 1.5708
    c: Tangent(g7,g9) = 1.5708
    c: Equal(g6,g9)
    c: Coincident(g8,g6)
    c: Coincident(g8,g9)
    c: Block(g7)
    c: Block(g8)
    c: Weight(g10) = 1
    c: Equal(g10,g11)
    c: Equal(g10,g12)
    c: InternalAlignment(g10,g13)
    c: InternalAlignment(g11,g13)
    c: InternalAlignment(g12,g13)
    c: InternalAlignment(g14,g13)
    c: InternalAlignment(g15,g13)
    c: Weight(g16) = 1
    c: Equal(g16,g17)
    c: Equal(g16,g18)
    c: InternalAlignment(g16,g19)
    c: InternalAlignment(g17,g19)
    c: InternalAlignment(g18,g19)
    c: InternalAlignment(g20,g19)
    c: InternalAlignment(g21,g19)
    c: Block(g19)
    c: Block(g13)
    c: Weight(g22) = 1
    c: Equal(g22,g23)
    c: Equal(g22,g24)
    c: InternalAlignment(g22,g25)
    c: InternalAlignment(g23,g25)
    c: InternalAlignment(g24,g25)
    c: InternalAlignment(g26,g25)
    c: InternalAlignment(g27,g25)
    c: Weight(g28) = 1
    c: Equal(g28,g29)
    c: Equal(g28,g30)
    c: InternalAlignment(g28,g31)
    c: InternalAlignment(g29,g31)
    c: InternalAlignment(g30,g31)
    c: InternalAlignment(g32,g31)
    c: InternalAlignment(g33,g31)
    c: Block(g31)
    c: Block(g25)
    c: Weight(g34) = 1
    c: Equal(g34,g35)
    c: Equal(g34,g36)
    c: InternalAlignment(g34,g37)
    c: InternalAlignment(g35,g37)
    c: InternalAlignment(g36,g37)
    c: InternalAlignment(g38,g37)
    c: InternalAlignment(g39,g37)
    c: Weight(g40) = 1
    c: Equal(g40,g41)
    c: Equal(g40,g42)
    c: InternalAlignment(g40,g43)
    c: InternalAlignment(g41,g43)
    c: InternalAlignment(g42,g43)
    c: InternalAlignment(g44,g43)
    c: InternalAlignment(g45,g43)
    c: Block(g37)
    c: Block(g43)
    c: Coincident(g46,g4)
    c: Coincident(g46,g3)
    c: Horizontal(g46)
    c: Distance(g46) = 450
    c: Coincident(g47,g4)
    c: Coincident(g47,g3)
    c: Horizontal(g47)
    c: Horizontal(g48)
    c: Coincident(g2,g48)
    c: Block(g48)
    c: Coincident(g1,g48)
    c: Weight(g49) = 1
    c: Equal(g49,g50)
    c: Equal(g49,g51)
    c: InternalAlignment(g49,g52)
    c: InternalAlignment(g50,g52)
    c: InternalAlignment(g51,g52)
    c: InternalAlignment(g53,g52)
    c: InternalAlignment(g54,g52)
    c: Block(g52)
    c: Weight(g55) = 1
    c: Equal(g55,g56)
    c: Equal(g55,g57)
    c: InternalAlignment(g55,g58)
    c: InternalAlignment(g56,g58)
    c: InternalAlignment(g57,g58)
    c: InternalAlignment(g59,g58)
    c: InternalAlignment(g60,g58)
    c: Block(g58)
    c: Weight(g61) = 1
    c: Equal(g61,g62)
    c: Equal(g61,g63)
    c: InternalAlignment(g61,g64)
    c: InternalAlignment(g62,g64)
    c: InternalAlignment(g63,g64)
    c: InternalAlignment(g65,g64)
    c: InternalAlignment(g66,g64)
    c: Block(g64)
    c: Weight(g67) = 1
    c: Equal(g67,g68)
    c: Equal(g67,g69)
    c: InternalAlignment(g67,g70)
    c: InternalAlignment(g68,g70)
    c: InternalAlignment(g69,g70)
    c: InternalAlignment(g71,g70)
    c: InternalAlignment(g72,g70)
    c: Block(g70)
    c: Weight(g73) = 1
    c: Equal(g73,g74)
    c: Equal(g73,g75)
    c: InternalAlignment(g73,g76)
    c: InternalAlignment(g74,g76)
    c: InternalAlignment(g75,g76)
    c: InternalAlignment(g77,g76)
    c: InternalAlignment(g78,g76)
    c: Weight(g79) = 1
    c: Equal(g79,g80)
    c: Equal(g79,g81)
    c: InternalAlignment(g79,g82)
    c: InternalAlignment(g80,g82)
    c: InternalAlignment(g81,g82)
    c: InternalAlignment(g83,g82)
    c: InternalAlignment(g84,g82)
    c: Block(g76)
    c: Block(g82)
    c: Coincident(g85,g76)
    c: Coincident(g85,g82)
    c: Vertical(g85)
    c: Coincident(g86,g76)
    c: Coincident(g86,g58)
    c: Coincident(g87,g58)
    c: Coincident(g87,g82)
    c: Weight(g88) = 1
    c: Equal(g88,g89)
    c: Equal(g88,g90)
    c: InternalAlignment(g88,g91)
    c: InternalAlignment(g89,g91)
    c: InternalAlignment(g90,g91)
    c: InternalAlignment(g92,g91)
    c: InternalAlignment(g93,g91)
    c: Weight(g94) = 1
    c: Equal(g94,g95)
    c: Equal(g94,g96)
    c: InternalAlignment(g94,g97)
    c: InternalAlignment(g95,g97)
    c: InternalAlignment(g96,g97)
    c: InternalAlignment(g98,g97)
    c: InternalAlignment(g99,g97)
    c: Block(g91)
    c: Block(g97)
    c: Coincident(g100,g91)
    c: Coincident(g100,g97)
    c: Vertical(g100)
    c: Coincident(g101,g91)
    c: Coincident(g101,g52)
    c: Coincident(g102,g52)
    c: Coincident(g102,g97)
    c: Weight(g103) = 1
    c: Equal(g103,g104)
    c: Equal(g103,g105)
    c: InternalAlignment(g103,g106)
    c: InternalAlignment(g104,g106)
    c: InternalAlignment(g105,g106)
    c: InternalAlignment(g107,g106)
    c: InternalAlignment(g108,g106)
    c: Weight(g109) = 1
    c: Equal(g109,g110)
    c: Equal(g109,g111)
    c: InternalAlignment(g109,g112)
    c: InternalAlignment(g110,g112)
    c: InternalAlignment(g111,g112)
    c: InternalAlignment(g113,g112)
    c: InternalAlignment(g114,g112)
    c: Block(g106)
    c: Block(g112)
    c: Coincident(g115,g106)
    c: Coincident(g115,g112)
    c: Vertical(g115)
    c: Coincident(g116,g112)
    c: Coincident(g116,g70)
    c: Coincident(g117,g70)
    c: Coincident(g117,g106)
    c: Weight(g118) = 1
    c: Equal(g118,g119)
    c: Equal(g118,g120)
    c: InternalAlignment(g118,g121)
    c: InternalAlignment(g119,g121)
    c: InternalAlignment(g120,g121)
    c: InternalAlignment(g122,g121)
    c: InternalAlignment(g123,g121)
    c: Weight(g124) = 1
    c: Equal(g124,g125)
    c: Equal(g124,g126)
    c: InternalAlignment(g124,g127)
    c: InternalAlignment(g125,g127)
    c: InternalAlignment(g126,g127)
    c: InternalAlignment(g128,g127)
    c: InternalAlignment(g129,g127)
    c: Block(g121)
    c: Block(g127)
    c: Coincident(g130,g121)
    c: Coincident(g130,g127)
    c: Vertical(g130)
    c: Coincident(g131,g127)
    c: Coincident(g131,g64)
    c: Coincident(g132,g64)
    c: Coincident(g132,g121)
    c: Weight(g133) = 1
    c: Equal(g133,g134)
    c: Equal(g133,g135)
    c: InternalAlignment(g133,g136)
    c: InternalAlignment(g134,g136)
    c: InternalAlignment(g135,g136)
    c: InternalAlignment(g137,g136)
    c: InternalAlignment(g138,g136)
    c: Weight(g139) = 1
    c: Equal(g139,g140)
    c: Equal(g139,g141)
    c: InternalAlignment(g139,g142)
    c: InternalAlignment(g140,g142)
    c: InternalAlignment(g141,g142)
    c: InternalAlignment(g143,g142)
    c: InternalAlignment(g144,g142)
    c: Weight(g145) = 1
    c: Equal(g145,g146)
    c: Equal(g145,g147)
    c: InternalAlignment(g145,g148)
    c: InternalAlignment(g146,g148)
    c: InternalAlignment(g147,g148)
    c: InternalAlignment(g149,g148)
    c: InternalAlignment(g150,g148)
    c: Weight(g151) = 1
    c: Equal(g151,g152)
    c: Equal(g151,g153)
    c: InternalAlignment(g151,g154)
    c: InternalAlignment(g152,g154)
    c: InternalAlignment(g153,g154)
    c: InternalAlignment(g155,g154)
    c: InternalAlignment(g156,g154)
    c: Block(g154)
    c: Block(g148)
    c: Block(g142)
    c: Block(g136)
    c: Coincident(g157,g31)
    c: Coincident(g157,g154)
    c: Coincident(g158,g154)
    c: Coincident(g158,g148)
    c: Horizontal(g158)
    c: Coincident(g159,g148)
    c: Coincident(g159,g31)
    c: Vertical(g159)
    c: Coincident(g160,g25)
    c: Coincident(g160,g142)
    c: Vertical(g160)
    c: Coincident(g161,g142)
    c: Coincident(g161,g136)
    c: Horizontal(g161)
    c: Coincident(g162,g136)
    c: Coincident(g162,g25)
    c: Weight(g163) = 1
    c: Equal(g163,g164)
    c: Equal(g163,g165)
    c: InternalAlignment(g163,g166)
    c: InternalAlignment(g164,g166)
    c: InternalAlignment(g165,g166)
    c: InternalAlignment(g167,g166)
    c: InternalAlignment(g168,g166)
    c: Weight(g169) = 1
    c: Equal(g169,g170)
    c: Equal(g169,g171)
    c: InternalAlignment(g169,g172)
    c: InternalAlignment(g170,g172)
    c: InternalAlignment(g171,g172)
    c: InternalAlignment(g173,g172)
    c: InternalAlignment(g174,g172)
    c: Weight(g175) = 1
    c: Equal(g175,g176)
    c: Equal(g175,g177)
    c: InternalAlignment(g175,g178)
    c: InternalAlignment(g176,g178)
    c: InternalAlignment(g177,g178)
    c: InternalAlignment(g179,g178)
    c: InternalAlignment(g180,g178)
    c: Weight(g181) = 1
    c: Equal(g181,g182)
    c: Equal(g181,g183)
    c: InternalAlignment(g181,g184)
    c: InternalAlignment(g182,g184)
    c: InternalAlignment(g183,g184)
    c: InternalAlignment(g185,g184)
    c: InternalAlignment(g186,g184)
    c: Block(g184)
    c: Block(g178)
    c: Block(g172)
    c: Block(g166)
    c: Coincident(g187,g184)
    c: Coincident(g187,g178)
    c: Horizontal(g187)
    c: Coincident(g188,g178)
    c: Coincident(g188,g13)
    c: Vertical(g188)
    c: Coincident(g189,g19)
    c: Coincident(g189,g172)
    c: Vertical(g189)
    c: Coincident(g190,g172)
    c: Coincident(g190,g166)
    c: Horizontal(g190)
    c: Coincident(g191,g166)
    c: Coincident(g191,g19)
    c: Coincident(g192,g13)
    c: Weight(g193) = 1
    c: Equal(g193,g194)
    c: Equal(g193,g195)
    c: InternalAlignment(g193,g196)
    c: InternalAlignment(g194,g196)
    c: InternalAlignment(g195,g196)
    c: InternalAlignment(g197,g196)
    c: InternalAlignment(g198,g196)
    c: Weight(g199) = 1
    c: Equal(g199,g200)
    c: Equal(g199,g201)
    c: InternalAlignment(g199,g202)
    c: InternalAlignment(g200,g202)
    c: InternalAlignment(g201,g202)
    c: InternalAlignment(g203,g202)
    c: InternalAlignment(g204,g202)
    c: Block(g202)
    c: Block(g196)
    c: Coincident(g205,g202)
    c: Coincident(g205,g37)
    c: Coincident(g206,g37)
    c: Coincident(g206,g196)
    c: Coincident(g207,g196)
    c: Coincident(g207,g202)
    c: Vertical(g207)
    c: Weight(g208) = 1
    c: Equal(g208,g209)
    c: Equal(g208,g210)
    c: InternalAlignment(g208,g211)
    c: InternalAlignment(g209,g211)
    c: InternalAlignment(g210,g211)
    c: InternalAlignment(g212,g211)
    c: InternalAlignment(g213,g211)
    c: Weight(g214) = 1
    c: Equal(g214,g215)
    c: Equal(g214,g216)
    c: InternalAlignment(g214,g217)
    c: InternalAlignment(g215,g217)
    c: InternalAlignment(g216,g217)
    c: InternalAlignment(g218,g217)
    c: InternalAlignment(g219,g217)
    c: Block(g217)
    c: Block(g211)
    c: Coincident(g220,g211)
    c: Coincident(g220,g43)
    c: Coincident(g221,g43)
    c: Coincident(g221,g217)
    c: Coincident(g222,g217)
    c: Coincident(g222,g211)
    c: Vertical(g222)
    c: Horizontal(g223)
    c: Block(g223)
    c: Vertical(g224)
    c: Block(g224)
    c: Block(g225)
    c: Weight(g226) = 1
    c: Equal(g226,g227)
    c: Equal(g226,g228)
    c: InternalAlignment(g226,g229)
    c: InternalAlignment(g227,g229)
    c: InternalAlignment(g228,g229)
    c: InternalAlignment(g230,g229)
    c: InternalAlignment(g231,g229)
    c: Weight(g232) = 1
    c: Equal(g232,g233)
    c: Equal(g232,g234)
    c: InternalAlignment(g232,g235)
    c: InternalAlignment(g233,g235)
    c: InternalAlignment(g234,g235)
    c: InternalAlignment(g236,g235)
    c: InternalAlignment(g237,g235)
    c: Weight(g238) = 1
    c: Equal(g238,g239)
    c: Equal(g238,g240)
    c: InternalAlignment(g238,g241)
    c: InternalAlignment(g239,g241)
    c: InternalAlignment(g240,g241)
    c: InternalAlignment(g242,g241)
    c: InternalAlignment(g243,g241)
    c: Weight(g244) = 1
    c: Equal(g244,g245)
    c: Equal(g244,g246)
    c: InternalAlignment(g244,g247)
    c: InternalAlignment(g245,g247)
    c: InternalAlignment(g246,g247)
    c: InternalAlignment(g248,g247)
    c: InternalAlignment(g249,g247)
    c: Block(g229)
    c: Block(g235)
    c: Block(g241)
    c: Block(g247)
    c: Coincident(g250,g235)
    c: Coincident(g250,g229)
    c: Horizontal(g250)
    c: Block(g192)
    c: Weight(g251) = 1
    c: Equal(g251,g252)
    c: Equal(g251,g253)
    c: InternalAlignment(g251,g254)
    c: InternalAlignment(g252,g254)
    c: InternalAlignment(g253,g254)
    c: InternalAlignment(g255,g254)
    c: InternalAlignment(g256,g254)
    c: Weight(g257) = 1
    c: Equal(g257,g258)
    c: Equal(g257,g259)
    c: InternalAlignment(g257,g260)
    c: InternalAlignment(g258,g260)
    c: InternalAlignment(g259,g260)
    c: InternalAlignment(g261,g260)
    c: InternalAlignment(g262,g260)
    c: Block(g254)
    c: Block(g260)
    c: Coincident(g263,g254)
    c: Coincident(g263,g260)
    c: Weight(g264) = 1
    c: Equal(g264,g265)
    c: Equal(g264,g266)
    c: InternalAlignment(g264,g267)
    c: InternalAlignment(g265,g267)
    c: InternalAlignment(g266,g267)
    c: InternalAlignment(g268,g267)
    c: InternalAlignment(g269,g267)
    c: Weight(g270) = 1
    c: Equal(g270,g271)
    c: Equal(g270,g272)
    c: InternalAlignment(g270,g273)
    c: InternalAlignment(g271,g273)
    c: InternalAlignment(g272,g273)
    c: InternalAlignment(g274,g273)
    c: InternalAlignment(g275,g273)
    c: Weight(g276) = 1
    c: Equal(g276,g277)
    c: Equal(g276,g278)
    c: InternalAlignment(g276,g279)
    c: InternalAlignment(g277,g279)
    c: InternalAlignment(g278,g279)
    c: InternalAlignment(g280,g279)
    c: InternalAlignment(g281,g279)
    c: Block(g279)
    c: Block(g273)
    c: Block(g267)
    c: Coincident(g282,g273)
    c: Coincident(g282,g267)
    c: Coincident(g283,g267)
    c: Coincident(g283,g279)
    c: Vertical(g283)
    c: Coincident(g284,g279)
    c: Coincident(g284,g273)
    c: Horizontal(g284)
    c: Weight(g285) = 1
    c: Equal(g285,g286)
    c: InternalAlignment(g285,g287)
    c: InternalAlignment(g286,g287)
    c: InternalAlignment(g288,g287)
    c: InternalAlignment(g289,g287)
    c: Weight(g290) = 1
    c: InternalAlignment(g291,g293)
    c: InternalAlignment(g292,g293)
    c: InternalAlignment(g294,g293)
    c: InternalAlignment(g295,g293)
    c: Weight(g296) = 1
    c: Equal(g296,g297)
    c: Equal(g296,g298)
    c: InternalAlignment(g296,g299)
    c: InternalAlignment(g297,g299)
    c: InternalAlignment(g298,g299)
    c: InternalAlignment(g300,g299)
    c: InternalAlignment(g301,g299)
    c: Equal(g302,g303)
    c: Equal(g302,g304)
    c: InternalAlignment(g302,g305)
    c: InternalAlignment(g303,g305)
    c: InternalAlignment(g304,g305)
    c: InternalAlignment(g306,g305)
    c: InternalAlignment(g307,g305)
    c: Block(g293)
    c: Block(g299)
    c: Block(g305)
    c: Block(g287)
    c: Coincident(g308,g287)
    c: Coincident(g308,g293)
    c: Horizontal(g308)
    c: Coincident(g309,g293)
    c: Coincident(g309,g299)
    c: Vertical(g309)
    c: Coincident(g310,g299)
    c: Coincident(g310,g305)
    c: Horizontal(g310)
    c: Coincident(g311,g305)
    c: Coincident(g311,g287)
    c: Weight(g312) = 1
    c: Equal(g312,g313)
    c: Equal(g312,g314)
    c: InternalAlignment(g312,g315)
    c: InternalAlignment(g313,g315)
    c: InternalAlignment(g314,g315)
    c: InternalAlignment(g316,g315)
    c: InternalAlignment(g317,g315)
    c: Weight(g318) = 1
    c: Equal(g318,g319)
    c: Equal(g318,g320)
    c: InternalAlignment(g318,g321)
    c: InternalAlignment(g319,g321)
    c: InternalAlignment(g320,g321)
    c: InternalAlignment(g322,g321)
    c: InternalAlignment(g323,g321)
    c: Weight(g324) = 1
    c: Equal(g324,g325)
    c: Equal(g324,g326)
    c: InternalAlignment(g324,g327)
    c: InternalAlignment(g325,g327)
    c: InternalAlignment(g326,g327)
    c: InternalAlignment(g328,g327)
    c: InternalAlignment(g329,g327)
    c: Block(g327)
    c: Block(g321)
    c: Block(g315)
    c: Coincident(g330,g327)
    c: Coincident(g330,g321)
    c: Horizontal(g330)
    c: Coincident(g331,g321)
    c: Coincident(g331,g315)
    c: Vertical(g331)
    c: Coincident(g332,g315)
    c: Coincident(g332,g327)
    c: InternalAlignment(g333,g334)
    c: InternalAlignment(g335,g334)
    c: InternalAlignment(g336,g334)
    c: Block(g334)
    c: Equal(g337,g338)
    c: Equal(g337,g339)
    c: InternalAlignment(g337,g340)
    c: InternalAlignment(g338,g340)
    c: InternalAlignment(g339,g340)
    c: InternalAlignment(g341,g340)
    c: InternalAlignment(g342,g340)
    c: Block(g340)
    c: Coincident(g343,g334)
    c: Horizontal(g343)
    c: Block(g343)
    c: Coincident(g344,g334)
    c: Coincident(g344,g260)
    c: Vertical(g344)
    c: Coincident(g345,g340)
    c: Coincident(g345,g254)
    c: Vertical(g345)
    c: Coincident(g347,g5)
    c: Coincident(g348,g5)
    c: Block(g346)
    c: Block(g5)
    c: Block(g348)
    c: Block(g347)
    c: Distance(g344) = 119.89
FEATURE [Sketcher::SketchObject] Sketch001
  FullyConstrained = true
  MapMode = 4
  Placement = pos=(0,0,0) rot=(0.57735,0.57735,0.57735;2.0944rad)
  Support = -> [Sketch]
  sketch-geometry (46):
    g0: BSplineCurve PolesCount=3 KnotsCount=2 Degree=2 IsPeriodic=0
    g1: ArcOfCircle CenterX=73.1223 CenterY=-32.291 CenterZ=0 NormalX=0 NormalY=0 NormalZ=1 AngleXU=0 Radius=13 StartAngle=5.92268 EndAngle=9.06428
    g2: ArcOfCircle CenterX=66.7816 CenterY=-49.1439 CenterZ=0 NormalX=0 NormalY=0 NormalZ=1 AngleXU=0 Radius=13 StartAngle=2.78068 EndAngle=5.92131
    g3: ArcOfCircle CenterX=55.9263 CenterY=-78.1807 CenterZ=0 NormalX=0 NormalY=0 NormalZ=1 AngleXU=0 Radius=13 StartAngle=5.92268 EndAngle=9.06428
    g4: ArcOfCircle CenterX=49.5884 CenterY=-95.0342 CenterZ=0 NormalX=0 NormalY=0 NormalZ=1 AngleXU=0 Radius=13 StartAngle=2.78068 EndAngle=5.92131
    g5: ArcOfCircle CenterX=38.7206 CenterY=-124.067 CenterZ=0 NormalX=0 NormalY=0 NormalZ=1 AngleXU=0 Radius=13 StartAngle=5.92268 EndAngle=9.06428
    g6: ArcOfCircle CenterX=32.3875 CenterY=-140.92 CenterZ=0 NormalX=0 NormalY=0 NormalZ=1 AngleXU=0 Radius=13 StartAngle=2.78068 EndAngle=5.92131
    g7: ArcOfCircle CenterX=21.4715 CenterY=-169.934 CenterZ=0 NormalX=0 NormalY=0 NormalZ=1 AngleXU=0 Radius=13 StartAngle=5.92268 EndAngle=9.06428
    g8: ArcOfCircle CenterX=15.1336 CenterY=-186.787 CenterZ=0 NormalX=0 NormalY=0 NormalZ=1 AngleXU=0 Radius=13 StartAngle=2.78068 EndAngle=5.92131
    g9-g12: Circle x4 (B-spline internal-alignment scaffolding for g13; pole/knot coordinates omitted)
    g13: BSplineCurve PolesCount=4 KnotsCount=2 Degree=3 IsPeriodic=0
    g14: GeomPoint X=28.8094 Y=-19.0875 Z=0
    g15: GeomPoint X=47.0443 Y=-50.4712 Z=0
    g16: Circle CenterX=53.5586 CenterY=-23.2695 CenterZ=0 NormalX=0 NormalY=0 NormalZ=1 AngleXU=0 Radius=3.24518
    g17: Circle CenterX=-195.441 CenterY=-127.082 CenterZ=0 NormalX=0 NormalY=0 NormalZ=1 AngleXU=0 Radius=1
    g18: Circle CenterX=-8.24091 CenterY=-197.481 CenterZ=0 NormalX=0 NormalY=0 NormalZ=1 AngleXU=0 Radius=1
    g19: Circle CenterX=12.8789 CenterY=-141.321 CenterZ=0 NormalX=0 NormalY=0 NormalZ=1 AngleXU=0 Radius=1
    g20: BSplineCurve PolesCount=3 KnotsCount=2 Degree=2 IsPeriodic=0
    g21: GeomPoint X=-195.441 Y=-127.082 Z=0
    g22: GeomPoint X=12.8789 Y=-141.321 Z=0
    g23: Circle CenterX=-12.8016 CenterY=-179.036 CenterZ=0 NormalX=0 NormalY=0 NormalZ=1 AngleXU=0 Radius=10.5072
    g24: Circle CenterX=0.933922 CenterY=-166.43 CenterZ=0 NormalX=0 NormalY=0 NormalZ=1 AngleXU=0 Radius=3.26661
    g25: Circle CenterX=-33.5518 CenterY=-176.44 CenterZ=0 NormalX=0 NormalY=0 NormalZ=1 AngleXU=0 Radius=5.64388
    g26: Circle CenterX=-47.2366 CenterY=-173.859 CenterZ=0 NormalX=0 NormalY=0 NormalZ=1 AngleXU=0 Radius=3.01653
    g27: Circle CenterX=-56.2595 CenterY=-171.456 CenterZ=0 NormalX=0 NormalY=0 NormalZ=1 AngleXU=0 Radius=2.12826
    g28: ArcOfCircle CenterX=51.2151 CenterY=-198.473 CenterZ=0 NormalX=0 NormalY=0 NormalZ=1 AngleXU=0 Radius=20 StartAngle=2.78189 EndAngle=4.35269
    g29: LineSegment StartX=32.4951 StartY=-191.433 StartZ=0 EndX=94.6578 EndY=-26.1352 EndZ=0
    g30: LineSegment StartX=43.1192 StartY=-220.001 StartZ=0 EndX=-196.497 EndY=-129.89 EndZ=0
    g31: LineSegment StartX=43.1192 StartY=-220.001 StartZ=0 EndX=44.1752 EndY=-217.193 EndZ=0
    g32: LineSegment StartX=117.223 StartY=-19.0875 StartZ=0 EndX=117.223 EndY=-16.0875 EndZ=0
    g33: LineSegment StartX=117.223 StartY=-16.0875 StartZ=0 EndX=17.2232 EndY=-16.0875 EndZ=0
    g34: LineSegment StartX=17.2232 StartY=-16.0875 StartZ=0 EndX=17.2232 EndY=-19.0875 EndZ=0
    g35: LineSegment StartX=28.8094 StartY=-19.0875 StartZ=0 EndX=17.2232 EndY=-19.0875 EndZ=0
    g36: LineSegment StartX=47.0443 StartY=-50.4712 StartZ=0 EndX=12.8789 EndY=-141.321 EndZ=0
    g37: LineSegment StartX=-195.441 StartY=-127.082 StartZ=0 EndX=-196.497 EndY=-129.89 EndZ=0
    g38: LineSegment StartX=85.2866 StartY=-36.8766 StartZ=0 EndX=78.9396 EndY=-53.7463 EndZ=0
    g39: LineSegment StartX=60.9579 StartY=-27.7053 StartZ=0 EndX=54.6191 EndY=-44.5532 EndZ=0
    g40: LineSegment StartX=68.0907 StartY=-82.7664 StartZ=0 EndX=61.7465 EndY=-99.6365 EndZ=0
    g41: LineSegment StartX=43.7619 StartY=-73.595 StartZ=0 EndX=37.426 EndY=-90.4435 EndZ=0
    g42: LineSegment StartX=50.885 StartY=-128.652 StartZ=0 EndX=44.5456 EndY=-145.522 EndZ=0
    g43: LineSegment StartX=26.5562 StartY=-119.481 StartZ=0 EndX=20.2251 EndY=-136.329 EndZ=0
    g44: LineSegment StartX=9.3071 StartY=-165.349 StartZ=0 EndX=2.97115 EndY=-182.197 EndZ=0
    g45: LineSegment StartX=33.6358 StartY=-174.52 StartZ=0 EndX=27.2917 EndY=-191.39 EndZ=0
  constraints (71):
    c: Block(g0)
    c: Block(g1)
    c: Block(g2)
    c: Block(g4)
    c: Block(g3)
    c: Block(g6)
    c: Block(g5)
    c: Block(g8)
    c: Block(g7)
    c: Weight(g9) = 1
    c: Equal(g9,g10)
    c: Equal(g9,g11)
    c: Equal(g9,g12)
    c: InternalAlignment(g9-g12 -> g13) x4
    c: InternalAlignment(g14,g13)
    c: InternalAlignment(g15,g13)
    c: Block(g16)
    c: Weight(g17) = 1
    c: Equal(g17,g18)
    c: Equal(g17,g19)
    c: InternalAlignment(g17,g20)
    c: InternalAlignment(g18,g20)
    c: InternalAlignment(g19,g20)
    c: InternalAlignment(g21,g20)
    c: InternalAlignment(g22,g20)
    c: Block(g20)
    c: Block(g23)
    c: Block(g24)
    c: Block(g25)
    c: Block(g26)
    c: Block(g27)
    c: Block(g28)
    c: Coincident(g29,g28)
    c: Coincident(g29,g0)
    c: Block(g13)
    c: Coincident(g31,g30)
    c: Coincident(g31,g28)
    c: Block(g31)
    c: Coincident(g32,g0)
    c: Vertical(g32)
    c: Coincident(g33,g32)
    c: Horizontal(g33)
    c: Coincident(g34,g33)
    c: Vertical(g34)
    c: Block(g33)
    c: Coincident(g35,g13)
    c: Coincident(g35,g34)
    c: Horizontal(g35)
    c: Coincident(g36,g13)
    c: Coincident(g36,g20)
    c: Coincident(g37,g20)
    c: Coincident(g37,g30)
    c: Block(g30)
    c: Coincident(g38,g1)
    c: Coincident(g38,g2)
    c: Coincident(g39,g1)
    c: Coincident(g39,g2)
    c: Coincident(g40,g3)
    c: Coincident(g40,g4)
    c: Coincident(g41,g3)
    c: Coincident(g41,g4)
    c: Coincident(g42,g5)
    c: Coincident(g42,g6)
    c: Coincident(g43,g5)
    c: Coincident(g43,g6)
    c: Coincident(g44,g7)
    c: Coincident(g44,g8)
    c: Coincident(g45,g7)
    c: Coincident(g45,g8)
    c: Distance(g30) = 256
    c: Distance(g33) = 100
FEATURE [Part::Extrusion] Extrude002
  Base = -> Sketch001
  Dir = (1,0,0)
  DirMode = 2
  FaceMakerClass = Part::FaceMakerBullseye
  LengthFwd = 8
  LengthRev = 0
  Solid = true
  Symmetric = false
FEATURE [Sketcher::SketchObject] Sketch002
  FullyConstrained = true
  sketch-geometry (20):
    g0: LineSegment StartX=-2.77179 StartY=-200.304 StartZ=0 EndX=5.22821 EndY=-200.304 EndZ=0
    g1: LineSegment StartX=5.22821 StartY=-200.304 StartZ=0 EndX=5.22821 EndY=-197.304 EndZ=0
    g2: LineSegment StartX=-2.77179 StartY=-200.304 StartZ=0 EndX=-2.77179 EndY=-197.304 EndZ=0
    g3: LineSegment StartX=5.22821 StartY=-197.304 StartZ=0 EndX=8.22821 EndY=-197.304 EndZ=0
    g4: LineSegment StartX=-2.77179 StartY=-197.304 StartZ=0 EndX=-5.77179 EndY=-197.304 EndZ=0
    g5: LineSegment StartX=19.2282 StartY=-203.304 StartZ=0 EndX=19.2282 EndY=-206.304 EndZ=0
    g6: LineSegment StartX=-16.7718 StartY=-203.304 StartZ=0 EndX=-16.7718 EndY=-206.304 EndZ=0
    g7: LineSegment StartX=-16.7718 StartY=-206.304 StartZ=0 EndX=19.2282 EndY=-206.304 EndZ=0
    g8: Circle CenterX=-16.7718 CenterY=-203.304 CenterZ=0 NormalX=0 NormalY=0 NormalZ=1 AngleXU=0 Radius=1
    g9: Circle CenterX=-5.77179 CenterY=-203.304 CenterZ=0 NormalX=0 NormalY=0 NormalZ=1 AngleXU=0 Radius=1
    g10: Circle CenterX=-5.77179 CenterY=-197.304 CenterZ=0 NormalX=0 NormalY=0 NormalZ=1 AngleXU=0 Radius=1
    g11: BSplineCurve PolesCount=3 KnotsCount=2 Degree=2 IsPeriodic=0
    g12: GeomPoint X=-16.7718 Y=-203.304 Z=0
    g13: GeomPoint X=-5.77179 Y=-197.304 Z=0
    g14: Circle CenterX=19.2282 CenterY=-203.304 CenterZ=0 NormalX=0 NormalY=0 NormalZ=1 AngleXU=0 Radius=1
    g15: Circle CenterX=8.22821 CenterY=-203.304 CenterZ=0 NormalX=0 NormalY=0 NormalZ=1 AngleXU=0 Radius=1
    g16: Circle CenterX=8.22821 CenterY=-197.304 CenterZ=0 NormalX=0 NormalY=0 NormalZ=1 AngleXU=0 Radius=1
    g17: BSplineCurve PolesCount=3 KnotsCount=2 Degree=2 IsPeriodic=0
    g18: GeomPoint X=19.2282 Y=-203.304 Z=0
    g19: GeomPoint X=8.22821 Y=-197.304 Z=0
  constraints (41):
    c: Horizontal(g0)
    c: Distance(g0) = 8
    c: Coincident(g1,g0)
    c: Vertical(g1)
    c: Distance(g1) = 3
    c: Coincident(g2,g0)
    c: Vertical(g2)
    c: Distance(g2) = 3
    c: Coincident(g3,g1)
    c: Horizontal(g3)
    c: Distance(g3) = 3
    c: Coincident(g4,g2)
    c: Horizontal(g4)
    c: Distance(g4) = 3
    c: Vertical(g5)
    c: Vertical(g6)
    c: Coincident(g7,g6)
    c: Coincident(g7,g5)
    c: Weight(g8) = 1
    c: Equal(g8,g9)
    c: Equal(g8,g10)
    c: Coincident(g11,g4)
    c: InternalAlignment(g8,g11)
    c: InternalAlignment(g9,g11)
    c: InternalAlignment(g10,g11)
    c: InternalAlignment(g12,g11)
    c: InternalAlignment(g13,g11)
    c: Coincident(g17,g5)
    c: Weight(g14) = 1
    c: Equal(g14,g15)
    c: Equal(g14,g16)
    c: Coincident(g17,g3)
    c: InternalAlignment(g14,g17)
    c: InternalAlignment(g15,g17)
    c: InternalAlignment(g16,g17)
    c: InternalAlignment(g18,g17)
    c: InternalAlignment(g19,g17)
    c: Block(g7)
    c: Block(g17)
    c: Block(g11)
    c: Block(g6)
FEATURE [Part::Extrusion] Extrude003
  Base = -> Sketch002
  Dir = (0,0,1)
  DirMode = 2
  FaceMakerClass = Part::FaceMakerBullseye
  LengthFwd = 260
  LengthRev = 0
  Solid = true
  Symmetric = false
FEATURE [Sketcher::SketchObject] Sketch003
  FullyConstrained = false
  sketch-geometry (379):
    g0: LineSegment StartX=-42.9272 StartY=136.221 StartZ=0 EndX=-42.9272 EndY=-103.779 EndZ=0
    g1: LineSegment StartX=407.073 StartY=136.221 StartZ=0 EndX=407.073 EndY=-103.779 EndZ=0
    g2: ArcOfCircle CenterX=-26.9272 CenterY=-83.7794 CenterZ=0 NormalX=0 NormalY=0 NormalZ=1 AngleXU=0 Radius=8 StartAngle=3.14159 EndAngle=6.28319
    g3: ArcOfCircle CenterX=391.073 CenterY=-83.7794 CenterZ=0 NormalX=0 NormalY=0 NormalZ=1 AngleXU=0 Radius=8 StartAngle=3.14159 EndAngle=6.28319
    g4: Circle CenterX=175.022 CenterY=27.0628 CenterZ=0 NormalX=0 NormalY=0 NormalZ=1 AngleXU=0 Radius=1
    g5: Circle CenterX=179.022 CenterY=24.8665 CenterZ=0 NormalX=0 NormalY=0 NormalZ=1 AngleXU=0 Radius=1
    g6: Circle CenterX=179.022 CenterY=27.0628 CenterZ=0 NormalX=0 NormalY=0 NormalZ=1 AngleXU=0 Radius=1
    g7: BSplineCurve PolesCount=3 KnotsCount=2 Degree=2 IsPeriodic=0
    g8: GeomPoint X=175.022 Y=27.0628 Z=0
    g9: GeomPoint X=179.022 Y=27.0628 Z=0
    g10: Circle CenterX=189.124 CenterY=27.0628 CenterZ=0 NormalX=0 NormalY=0 NormalZ=1 AngleXU=0 Radius=1
    g11: Circle CenterX=185.124 CenterY=24.8665 CenterZ=0 NormalX=0 NormalY=0 NormalZ=1 AngleXU=0 Radius=1
    g12: Circle CenterX=185.124 CenterY=27.0628 CenterZ=0 NormalX=0 NormalY=0 NormalZ=1 AngleXU=0 Radius=1
    g13: BSplineCurve PolesCount=3 KnotsCount=2 Degree=2 IsPeriodic=0
    g14: GeomPoint X=189.124 Y=27.0628 Z=0
    g15: GeomPoint X=185.124 Y=27.0628 Z=0
    g16: Circle CenterX=175.022 CenterY=5.37834 CenterZ=0 NormalX=0 NormalY=0 NormalZ=1 AngleXU=0 Radius=1
    g17: Circle CenterX=179.022 CenterY=7.57463 CenterZ=0 NormalX=0 NormalY=0 NormalZ=1 AngleXU=0 Radius=1
    g18: Circle CenterX=179.022 CenterY=5.34704 CenterZ=0 NormalX=0 NormalY=0 NormalZ=1 AngleXU=0 Radius=1
    g19: BSplineCurve PolesCount=3 KnotsCount=2 Degree=2 IsPeriodic=0
    g20: GeomPoint X=175.022 Y=5.37834 Z=0
    g21: GeomPoint X=179.022 Y=5.34704 Z=0
    g22: Circle CenterX=189.124 CenterY=5.37834 CenterZ=0 NormalX=0 NormalY=0 NormalZ=1 AngleXU=0 Radius=1
    g23: Circle CenterX=185.124 CenterY=7.57463 CenterZ=0 NormalX=0 NormalY=0 NormalZ=1 AngleXU=0 Radius=1
    g24: Circle CenterX=185.124 CenterY=5.34704 CenterZ=0 NormalX=0 NormalY=0 NormalZ=1 AngleXU=0 Radius=1
    g25: BSplineCurve PolesCount=3 KnotsCount=2 Degree=2 IsPeriodic=0
    g26: GeomPoint X=189.124 Y=5.37834 Z=0
    g27: GeomPoint X=185.124 Y=5.34704 Z=0
    g28: Circle CenterX=165.871 CenterY=18.1458 CenterZ=0 NormalX=0 NormalY=0 NormalZ=1 AngleXU=0 Radius=1
    g29: Circle CenterX=169.377 CenterY=16.2206 CenterZ=0 NormalX=0 NormalY=0 NormalZ=1 AngleXU=0 Radius=1
    g30: Circle CenterX=165.871 CenterY=14.2954 CenterZ=0 NormalX=0 NormalY=0 NormalZ=1 AngleXU=0 Radius=1
    g31: BSplineCurve PolesCount=3 KnotsCount=2 Degree=2 IsPeriodic=0
    g32: GeomPoint X=165.871 Y=18.1458 Z=0
    g33: GeomPoint X=165.871 Y=14.2954 Z=0
    g34: Circle CenterX=198.275 CenterY=18.1458 CenterZ=0 NormalX=0 NormalY=0 NormalZ=1 AngleXU=0 Radius=1
    g35: Circle CenterX=194.768 CenterY=16.2206 CenterZ=0 NormalX=0 NormalY=0 NormalZ=1 AngleXU=0 Radius=1
    g36: Circle CenterX=198.275 CenterY=14.2954 CenterZ=0 NormalX=0 NormalY=0 NormalZ=1 AngleXU=0 Radius=1
    g37: BSplineCurve PolesCount=3 KnotsCount=2 Degree=2 IsPeriodic=0
    g38: GeomPoint X=198.275 Y=18.1458 Z=0
    g39: GeomPoint X=198.275 Y=14.2954 Z=0
    g40: LineSegment StartX=407.073 StartY=-103.779 StartZ=0 EndX=-42.9272 EndY=-103.779 EndZ=0
    g41: Circle CenterX=125.607 CenterY=54.1951 CenterZ=0 NormalX=0 NormalY=0 NormalZ=1 AngleXU=0 Radius=1
    g42: Circle CenterX=139.632 CenterY=46.4944 CenterZ=0 NormalX=0 NormalY=0 NormalZ=1 AngleXU=0 Radius=1
    g43: Circle CenterX=127.326 CenterY=56.7187 CenterZ=0 NormalX=0 NormalY=0 NormalZ=1 AngleXU=0 Radius=1
    g44: BSplineCurve PolesCount=3 KnotsCount=2 Degree=2 IsPeriodic=0
    g45: GeomPoint X=125.607 Y=54.1951 Z=0
    g46: GeomPoint X=127.326 Y=56.7187 Z=0
    g47: Circle CenterX=236.821 CenterY=56.7187 CenterZ=0 NormalX=0 NormalY=0 NormalZ=1 AngleXU=0 Radius=1
    g48: Circle CenterX=224.513 CenterY=46.4944 CenterZ=0 NormalX=0 NormalY=0 NormalZ=1 AngleXU=0 Radius=1
    g49: Circle CenterX=238.538 CenterY=54.1951 CenterZ=0 NormalX=0 NormalY=0 NormalZ=1 AngleXU=0 Radius=1
    g50: BSplineCurve PolesCount=3 KnotsCount=2 Degree=2 IsPeriodic=0
    g51: GeomPoint X=236.821 Y=56.7187 Z=0
    g52: GeomPoint X=238.538 Y=54.1951 Z=0
    g53: Circle CenterX=238.538 CenterY=-21.7539 CenterZ=0 NormalX=0 NormalY=0 NormalZ=1 AngleXU=0 Radius=1
    g54: Circle CenterX=224.513 CenterY=-14.0532 CenterZ=0 NormalX=0 NormalY=0 NormalZ=1 AngleXU=0 Radius=1
    g55: Circle CenterX=236.821 CenterY=-24.2775 CenterZ=0 NormalX=0 NormalY=0 NormalZ=1 AngleXU=0 Radius=1
    g56: BSplineCurve PolesCount=3 KnotsCount=2 Degree=2 IsPeriodic=0
    g57: GeomPoint X=238.538 Y=-21.7539 Z=0
    g58: GeomPoint X=236.821 Y=-24.2775 Z=0
    g59: Circle CenterX=125.607 CenterY=-21.7539 CenterZ=0 NormalX=0 NormalY=0 NormalZ=1 AngleXU=0 Radius=1
    g60: Circle CenterX=139.632 CenterY=-14.0532 CenterZ=0 NormalX=0 NormalY=0 NormalZ=1 AngleXU=0 Radius=1
    g61: Circle CenterX=127.325 CenterY=-24.2775 CenterZ=0 NormalX=0 NormalY=0 NormalZ=1 AngleXU=0 Radius=1
    g62: BSplineCurve PolesCount=3 KnotsCount=2 Degree=2 IsPeriodic=0
    g63: GeomPoint X=125.607 Y=-21.7539 Z=0
    g64: GeomPoint X=127.325 Y=-24.2775 Z=0
    g65: Circle CenterX=302.996 CenterY=111.695 CenterZ=0 NormalX=0 NormalY=0 NormalZ=1 AngleXU=0 Radius=1
    g66: Circle CenterX=306.073 CenterY=114.251 CenterZ=0 NormalX=0 NormalY=0 NormalZ=1 AngleXU=0 Radius=1
    g67: Circle CenterX=306.073 CenterY=110.251 CenterZ=0 NormalX=0 NormalY=0 NormalZ=1 AngleXU=0 Radius=1
    g68: BSplineCurve PolesCount=3 KnotsCount=2 Degree=2 IsPeriodic=0
    g69: GeomPoint X=302.996 Y=111.695 Z=0
    g70: GeomPoint X=306.073 Y=110.251 Z=0
    g71: Circle CenterX=306.073 CenterY=95.2763 CenterZ=0 NormalX=0 NormalY=0 NormalZ=1 AngleXU=0 Radius=1
    g72: Circle CenterX=306.073 CenterY=91.2763 CenterZ=0 NormalX=0 NormalY=0 NormalZ=1 AngleXU=0 Radius=1
    g73: Circle CenterX=302.567 CenterY=89.3511 CenterZ=0 NormalX=0 NormalY=0 NormalZ=1 AngleXU=0 Radius=1
    g74: BSplineCurve PolesCount=3 KnotsCount=2 Degree=2 IsPeriodic=0
    g75: GeomPoint X=306.073 Y=95.2763 Z=0
    g76: GeomPoint X=302.567 Y=89.3511 Z=0
    g77: LineSegment StartX=306.073 StartY=110.251 StartZ=0 EndX=306.073 EndY=95.2763 EndZ=0
    g78: LineSegment StartX=302.996 StartY=111.695 StartZ=0 EndX=236.821 EndY=56.7187 EndZ=0
    g79: LineSegment StartX=238.538 StartY=54.1951 StartZ=0 EndX=302.567 EndY=89.3511 EndZ=0
    g80: Circle CenterX=61.1496 CenterY=111.695 CenterZ=0 NormalX=0 NormalY=0 NormalZ=1 AngleXU=0 Radius=1
    g81: Circle CenterX=58.0728 CenterY=114.251 CenterZ=0 NormalX=0 NormalY=0 NormalZ=1 AngleXU=0 Radius=1
    g82: Circle CenterX=58.0728 CenterY=110.251 CenterZ=0 NormalX=0 NormalY=0 NormalZ=1 AngleXU=0 Radius=1
    g83: BSplineCurve PolesCount=3 KnotsCount=2 Degree=2 IsPeriodic=0
    g84: GeomPoint X=61.1496 Y=111.695 Z=0
    g85: GeomPoint X=58.0728 Y=110.251 Z=0
    g86: Circle CenterX=61.5791 CenterY=89.3511 CenterZ=0 NormalX=0 NormalY=0 NormalZ=1 AngleXU=0 Radius=1
    g87: Circle CenterX=58.0728 CenterY=91.2763 CenterZ=0 NormalX=0 NormalY=0 NormalZ=1 AngleXU=0 Radius=1
    g88: Circle CenterX=58.0728 CenterY=95.2763 CenterZ=0 NormalX=0 NormalY=0 NormalZ=1 AngleXU=0 Radius=1
    g89: BSplineCurve PolesCount=3 KnotsCount=2 Degree=2 IsPeriodic=0
    g90: GeomPoint X=61.5791 Y=89.3511 Z=0
    g91: GeomPoint X=58.0728 Y=95.2763 Z=0
    g92: LineSegment StartX=58.0728 StartY=110.251 StartZ=0 EndX=58.0728 EndY=95.2763 EndZ=0
    g93: LineSegment StartX=61.1496 StartY=111.695 StartZ=0 EndX=127.326 EndY=56.7187 EndZ=0
    g94: LineSegment StartX=125.607 StartY=54.1951 StartZ=0 EndX=61.5791 EndY=89.3511 EndZ=0
    g95: Circle CenterX=61.5791 CenterY=-56.9099 CenterZ=0 NormalX=0 NormalY=0 NormalZ=1 AngleXU=0 Radius=1
    g96: Circle CenterX=58.0728 CenterY=-58.8351 CenterZ=0 NormalX=0 NormalY=0 NormalZ=1 AngleXU=0 Radius=1
    g97: Circle CenterX=58.0728 CenterY=-62.8351 CenterZ=0 NormalX=0 NormalY=0 NormalZ=1 AngleXU=0 Radius=1
    g98: BSplineCurve PolesCount=3 KnotsCount=2 Degree=2 IsPeriodic=0
    g99: GeomPoint X=61.5791 Y=-56.9099 Z=0
    g100: GeomPoint X=58.0728 Y=-62.8351 Z=0
    g101: Circle CenterX=58.0728 CenterY=-77.8102 CenterZ=0 NormalX=0 NormalY=0 NormalZ=1 AngleXU=0 Radius=1
    g102: Circle CenterX=58.0728 CenterY=-81.8102 CenterZ=0 NormalX=0 NormalY=0 NormalZ=1 AngleXU=0 Radius=1
    g103: Circle CenterX=61.1496 CenterY=-79.2541 CenterZ=0 NormalX=0 NormalY=0 NormalZ=1 AngleXU=0 Radius=1
    g104: BSplineCurve PolesCount=3 KnotsCount=2 Degree=2 IsPeriodic=0
    g105: GeomPoint X=58.0728 Y=-77.8102 Z=0
    g106: GeomPoint X=61.1496 Y=-79.2541 Z=0
    g107: LineSegment StartX=58.0728 StartY=-62.8351 StartZ=0 EndX=58.0728 EndY=-77.8102 EndZ=0
    g108: LineSegment StartX=61.1496 StartY=-79.2541 StartZ=0 EndX=127.325 EndY=-24.2775 EndZ=0
    g109: LineSegment StartX=125.607 StartY=-21.7539 StartZ=0 EndX=61.5791 EndY=-56.9099 EndZ=0
    g110: Circle CenterX=302.567 CenterY=-56.9099 CenterZ=0 NormalX=0 NormalY=0 NormalZ=1 AngleXU=0 Radius=1
    g111: Circle CenterX=306.073 CenterY=-58.8351 CenterZ=0 NormalX=0 NormalY=0 NormalZ=1 AngleXU=0 Radius=1
    g112: Circle CenterX=306.073 CenterY=-62.8351 CenterZ=0 NormalX=0 NormalY=0 NormalZ=1 AngleXU=0 Radius=1
    g113: BSplineCurve PolesCount=3 KnotsCount=2 Degree=2 IsPeriodic=0
    g114: GeomPoint X=302.567 Y=-56.9099 Z=0
    g115: GeomPoint X=306.073 Y=-62.8351 Z=0
    g116: Circle CenterX=302.996 CenterY=-79.2541 CenterZ=0 NormalX=0 NormalY=0 NormalZ=1 AngleXU=0 Radius=1
    g117: Circle CenterX=306.073 CenterY=-81.8102 CenterZ=0 NormalX=0 NormalY=0 NormalZ=1 AngleXU=0 Radius=1
    g118: Circle CenterX=306.073 CenterY=-77.8102 CenterZ=0 NormalX=0 NormalY=0 NormalZ=1 AngleXU=0 Radius=1
    g119: BSplineCurve PolesCount=3 KnotsCount=2 Degree=2 IsPeriodic=0
    g120: GeomPoint X=302.996 Y=-79.2541 Z=0
    g121: GeomPoint X=306.073 Y=-77.8102 Z=0
    g122: LineSegment StartX=306.073 StartY=-62.8351 StartZ=0 EndX=306.073 EndY=-77.8102 EndZ=0
    g123: LineSegment StartX=302.996 StartY=-79.2541 StartZ=0 EndX=236.821 EndY=-24.2775 EndZ=0
    g124: LineSegment StartX=238.538 StartY=-21.7539 StartZ=0 EndX=302.567 EndY=-56.9099 EndZ=0
    g125: Circle CenterX=61.6457 CenterY=-88.8112 CenterZ=0 NormalX=0 NormalY=0 NormalZ=1 AngleXU=0 Radius=1
    g126: Circle CenterX=58.0728 CenterY=-91.7794 CenterZ=0 NormalX=0 NormalY=0 NormalZ=1 AngleXU=0 Radius=1
    g127: Circle CenterX=63.9135 CenterY=-91.7794 CenterZ=0 NormalX=0 NormalY=0 NormalZ=1 AngleXU=0 Radius=1
    g128: BSplineCurve PolesCount=3 KnotsCount=2 Degree=2 IsPeriodic=0
    g129: GeomPoint X=61.6457 Y=-88.8112 Z=0
    g130: GeomPoint X=63.9135 Y=-91.7794 Z=0
    g131: Circle CenterX=179.022 CenterY=-85.8163 CenterZ=0 NormalX=0 NormalY=0 NormalZ=1 AngleXU=0 Radius=1
    g132: Circle CenterX=179.022 CenterY=-91.7794 CenterZ=0 NormalX=0 NormalY=0 NormalZ=1 AngleXU=0 Radius=1
    g133: Circle CenterX=171.895 CenterY=-91.7794 CenterZ=0 NormalX=0 NormalY=0 NormalZ=1 AngleXU=0 Radius=1
    g134: BSplineCurve PolesCount=3 KnotsCount=2 Degree=2 IsPeriodic=0
    g135: GeomPoint X=179.022 Y=-85.8163 Z=0
    g136: GeomPoint X=171.895 Y=-91.7794 Z=0
    g137: Circle CenterX=185.124 CenterY=-86.2028 CenterZ=0 NormalX=0 NormalY=0 NormalZ=1 AngleXU=0 Radius=1
    g138: Circle CenterX=185.124 CenterY=-91.7794 CenterZ=0 NormalX=0 NormalY=0 NormalZ=1 AngleXU=0 Radius=1
    g139: Circle CenterX=191.747 CenterY=-91.7794 CenterZ=0 NormalX=0 NormalY=0 NormalZ=1 AngleXU=0 Radius=1
    g140: BSplineCurve PolesCount=3 KnotsCount=2 Degree=2 IsPeriodic=0
    g141: GeomPoint X=185.124 Y=-86.2028 Z=0
    g142: GeomPoint X=191.747 Y=-91.7794 Z=0
    g143: Circle CenterX=299.888 CenterY=-86.6413 CenterZ=0 NormalX=0 NormalY=0 NormalZ=1 AngleXU=0 Radius=1
    g144: Circle CenterX=306.073 CenterY=-91.7794 CenterZ=0 NormalX=0 NormalY=0 NormalZ=1 AngleXU=0 Radius=1
    g145: Circle CenterX=298.776 CenterY=-91.7794 CenterZ=0 NormalX=0 NormalY=0 NormalZ=1 AngleXU=0 Radius=1
    g146: BSplineCurve PolesCount=3 KnotsCount=2 Degree=2 IsPeriodic=0
    g147: GeomPoint X=299.888 Y=-86.6413 Z=0
    g148: GeomPoint X=298.776 Y=-91.7794 Z=0
    g149: LineSegment StartX=189.124 StartY=5.37834 StartZ=0 EndX=299.888 EndY=-86.6413 EndZ=0
    g150: LineSegment StartX=298.776 StartY=-91.7794 StartZ=0 EndX=191.747 EndY=-91.7794 EndZ=0
    g151: LineSegment StartX=185.124 StartY=-86.2028 StartZ=0 EndX=185.124 EndY=5.34704 EndZ=0
    g152: LineSegment StartX=179.022 StartY=5.34704 StartZ=0 EndX=179.022 EndY=-85.8163 EndZ=0
    g153: LineSegment StartX=171.895 StartY=-91.7794 StartZ=0 EndX=63.9135 EndY=-91.7794 EndZ=0
    g154: LineSegment StartX=61.6457 StartY=-88.8112 StartZ=0 EndX=175.022 EndY=5.37834 EndZ=0
    g155: Circle CenterX=302.073 CenterY=124.221 CenterZ=0 NormalX=0 NormalY=0 NormalZ=1 AngleXU=0 Radius=1
    g156: Circle CenterX=306.073 CenterY=124.221 CenterZ=0 NormalX=0 NormalY=0 NormalZ=1 AngleXU=0 Radius=1
    g157: Circle CenterX=302.996 CenterY=121.665 CenterZ=0 NormalX=0 NormalY=0 NormalZ=1 AngleXU=0 Radius=1
    g158: BSplineCurve PolesCount=3 KnotsCount=2 Degree=2 IsPeriodic=0
    g159: GeomPoint X=302.073 Y=124.221 Z=0
    g160: GeomPoint X=302.996 Y=121.665 Z=0
    g161: Circle CenterX=189.124 CenterY=124.221 CenterZ=0 NormalX=0 NormalY=0 NormalZ=1 AngleXU=0 Radius=1
    g162: Circle CenterX=185.124 CenterY=124.221 CenterZ=0 NormalX=0 NormalY=0 NormalZ=1 AngleXU=0 Radius=1
    g163: Circle CenterX=185.124 CenterY=120.221 CenterZ=0 NormalX=0 NormalY=0 NormalZ=1 AngleXU=0 Radius=1
    g164: BSplineCurve PolesCount=3 KnotsCount=2 Degree=2 IsPeriodic=0
    g165: GeomPoint X=189.124 Y=124.221 Z=0
    g166: GeomPoint X=185.124 Y=120.221 Z=0
    g167: Circle CenterX=175.022 CenterY=124.221 CenterZ=0 NormalX=0 NormalY=0 NormalZ=1 AngleXU=0 Radius=1
    g168: Circle CenterX=179.022 CenterY=124.221 CenterZ=0 NormalX=0 NormalY=0 NormalZ=1 AngleXU=0 Radius=1
    g169: Circle CenterX=179.022 CenterY=120.221 CenterZ=0 NormalX=0 NormalY=0 NormalZ=1 AngleXU=0 Radius=1
    g170: BSplineCurve PolesCount=3 KnotsCount=2 Degree=2 IsPeriodic=0
    g171: GeomPoint X=175.022 Y=124.221 Z=0
    g172: GeomPoint X=179.022 Y=120.221 Z=0
    g173: Circle CenterX=62.0728 CenterY=124.221 CenterZ=0 NormalX=0 NormalY=0 NormalZ=1 AngleXU=0 Radius=1
    g174: Circle CenterX=58.0728 CenterY=124.221 CenterZ=0 NormalX=0 NormalY=0 NormalZ=1 AngleXU=0 Radius=1
    g175: Circle CenterX=61.1496 CenterY=121.665 CenterZ=0 NormalX=0 NormalY=0 NormalZ=1 AngleXU=0 Radius=1
    g176: BSplineCurve PolesCount=3 KnotsCount=2 Degree=2 IsPeriodic=0
    g177: GeomPoint X=62.0728 Y=124.221 Z=0
    g178: GeomPoint X=61.1496 Y=121.665 Z=0
    g179: LineSegment StartX=62.0728 StartY=124.221 StartZ=0 EndX=175.022 EndY=124.221 EndZ=0
    g180: LineSegment StartX=179.022 StartY=120.221 StartZ=0 EndX=179.022 EndY=27.0628 EndZ=0
    g181: LineSegment StartX=185.124 StartY=27.0628 StartZ=0 EndX=185.124 EndY=120.221 EndZ=0
    g182: LineSegment StartX=189.124 StartY=124.221 StartZ=0 EndX=302.073 EndY=124.221 EndZ=0
    g183: LineSegment StartX=302.996 StartY=121.665 StartZ=0 EndX=189.124 EndY=27.0628 EndZ=0
    g184: LineSegment StartX=175.022 StartY=27.0628 StartZ=0 EndX=61.1496 EndY=121.665 EndZ=0
    g185: Circle CenterX=61.5791 CenterY=75.4095 CenterZ=0 NormalX=0 NormalY=0 NormalZ=1 AngleXU=0 Radius=1
    g186: Circle CenterX=58.0728 CenterY=77.3346 CenterZ=0 NormalX=0 NormalY=0 NormalZ=1 AngleXU=0 Radius=1
    g187: Circle CenterX=58.0728 CenterY=73.3346 CenterZ=0 NormalX=0 NormalY=0 NormalZ=1 AngleXU=0 Radius=1
    g188: BSplineCurve PolesCount=3 KnotsCount=2 Degree=2 IsPeriodic=0
    g189: GeomPoint X=61.5791 Y=75.4095 Z=0
    g190: GeomPoint X=58.0728 Y=73.3346 Z=0
    g191: Circle CenterX=58.0728 CenterY=-40.8935 CenterZ=0 NormalX=0 NormalY=0 NormalZ=1 AngleXU=0 Radius=1
    g192: Circle CenterX=58.0728 CenterY=-44.8935 CenterZ=0 NormalX=0 NormalY=0 NormalZ=1 AngleXU=0 Radius=1
    g193: Circle CenterX=61.5791 CenterY=-42.9683 CenterZ=0 NormalX=0 NormalY=0 NormalZ=1 AngleXU=0 Radius=1
    g194: BSplineCurve PolesCount=3 KnotsCount=2 Degree=2 IsPeriodic=0
    g195: GeomPoint X=58.0728 Y=-40.8935 Z=0
    g196: GeomPoint X=61.5791 Y=-42.9683 Z=0
    g197: LineSegment StartX=61.5791 StartY=-42.9683 StartZ=0 EndX=165.871 EndY=14.2954 EndZ=0
    g198: LineSegment StartX=165.871 StartY=18.1458 StartZ=0 EndX=61.5791 EndY=75.4095 EndZ=0
    g199: LineSegment StartX=58.0728 StartY=73.3346 StartZ=0 EndX=58.0728 EndY=-40.8935 EndZ=0
    g200: Circle CenterX=302.567 CenterY=-42.9683 CenterZ=0 NormalX=0 NormalY=0 NormalZ=1 AngleXU=0 Radius=1
    g201: Circle CenterX=306.073 CenterY=-44.8935 CenterZ=0 NormalX=0 NormalY=0 NormalZ=1 AngleXU=0 Radius=1
    g202: Circle CenterX=306.073 CenterY=-40.8935 CenterZ=0 NormalX=0 NormalY=0 NormalZ=1 AngleXU=0 Radius=1
    g203: BSplineCurve PolesCount=3 KnotsCount=2 Degree=2 IsPeriodic=0
    g204: GeomPoint X=302.567 Y=-42.9683 Z=0
    g205: GeomPoint X=306.073 Y=-40.8935 Z=0
    g206: Circle CenterX=306.073 CenterY=73.3346 CenterZ=0 NormalX=0 NormalY=0 NormalZ=1 AngleXU=0 Radius=1
    g207: Circle CenterX=306.073 CenterY=77.3346 CenterZ=0 NormalX=0 NormalY=0 NormalZ=1 AngleXU=0 Radius=1
    g208: Circle CenterX=302.567 CenterY=75.4095 CenterZ=0 NormalX=0 NormalY=0 NormalZ=1 AngleXU=0 Radius=1
    g209: BSplineCurve PolesCount=3 KnotsCount=2 Degree=2 IsPeriodic=0
    g210: GeomPoint X=306.073 Y=73.3346 Z=0
    g211: GeomPoint X=302.567 Y=75.4095 Z=0
    g212: LineSegment StartX=302.567 StartY=-42.9683 StartZ=0 EndX=198.275 EndY=14.2954 EndZ=0
    g213: LineSegment StartX=198.275 StartY=18.1458 StartZ=0 EndX=302.567 EndY=75.4095 EndZ=0
    g214: LineSegment StartX=306.073 StartY=73.3346 StartZ=0 EndX=306.073 EndY=-40.8935 EndZ=0
    g215: LineSegment StartX=322.073 StartY=105.865 StartZ=0 EndX=328.643 EndY=105.865 EndZ=0
    g216: LineSegment StartX=318.073 StartY=120.221 StartZ=0 EndX=318.073 EndY=109.865 EndZ=0
    g217: LineSegment StartX=336.157 StartY=107.779 StartZ=0 EndX=362.567 EndY=122.294 EndZ=0
    g218: Circle CenterX=362.073 CenterY=124.221 CenterZ=0 NormalX=0 NormalY=0 NormalZ=1 AngleXU=0 Radius=1
    g219: Circle CenterX=366.073 CenterY=124.221 CenterZ=0 NormalX=0 NormalY=0 NormalZ=1 AngleXU=0 Radius=1
    g220: Circle CenterX=362.567 CenterY=122.294 CenterZ=0 NormalX=0 NormalY=0 NormalZ=1 AngleXU=0 Radius=1
    g221: BSplineCurve PolesCount=3 KnotsCount=2 Degree=2 IsPeriodic=0
    g222: GeomPoint X=362.073 Y=124.221 Z=0
    g223: GeomPoint X=362.567 Y=122.294 Z=0
    g224: Circle CenterX=322.073 CenterY=124.221 CenterZ=0 NormalX=0 NormalY=0 NormalZ=1 AngleXU=0 Radius=1
    g225: Circle CenterX=318.073 CenterY=124.221 CenterZ=0 NormalX=0 NormalY=0 NormalZ=1 AngleXU=0 Radius=1
    g226: Circle CenterX=318.073 CenterY=120.221 CenterZ=0 NormalX=0 NormalY=0 NormalZ=1 AngleXU=0 Radius=1
    g227: BSplineCurve PolesCount=3 KnotsCount=2 Degree=2 IsPeriodic=0
    g228: GeomPoint X=322.073 Y=124.221 Z=0
    g229: GeomPoint X=318.073 Y=120.221 Z=0
    g230: Circle CenterX=322.073 CenterY=105.865 CenterZ=0 NormalX=0 NormalY=0 NormalZ=1 AngleXU=0 Radius=1
    g231: Circle CenterX=318.073 CenterY=105.865 CenterZ=0 NormalX=0 NormalY=0 NormalZ=1 AngleXU=0 Radius=1
    g232: Circle CenterX=318.073 CenterY=109.865 CenterZ=0 NormalX=0 NormalY=0 NormalZ=1 AngleXU=0 Radius=1
    g233: BSplineCurve PolesCount=3 KnotsCount=2 Degree=2 IsPeriodic=0
    g234: GeomPoint X=322.073 Y=105.865 Z=0
    g235: GeomPoint X=318.073 Y=109.865 Z=0
    g236: Circle CenterX=336.157 CenterY=107.779 CenterZ=0 NormalX=0 NormalY=0 NormalZ=1 AngleXU=0 Radius=1
    g237: Circle CenterX=332.651 CenterY=105.853 CenterZ=0 NormalX=0 NormalY=0 NormalZ=1 AngleXU=0 Radius=1
    g238: Circle CenterX=328.643 CenterY=105.865 CenterZ=0 NormalX=0 NormalY=0 NormalZ=1 AngleXU=0 Radius=1
    g239: BSplineCurve PolesCount=3 KnotsCount=2 Degree=2 IsPeriodic=0
    g240: GeomPoint X=336.157 Y=107.779 Z=0
    g241: GeomPoint X=328.643 Y=105.865 Z=0
    g242: LineSegment StartX=322.073 StartY=124.221 StartZ=0 EndX=362.073 EndY=124.221 EndZ=0
    g243: Circle CenterX=371.567 CenterY=-80.8644 CenterZ=0 NormalX=0 NormalY=0 NormalZ=1 AngleXU=0 Radius=1
    g244: Circle CenterX=375.073 CenterY=-82.7896 CenterZ=0 NormalX=0 NormalY=0 NormalZ=1 AngleXU=0 Radius=1
    g245: Circle CenterX=375.073 CenterY=-78.7896 CenterZ=0 NormalX=0 NormalY=0 NormalZ=1 AngleXU=0 Radius=1
    g246: BSplineCurve PolesCount=3 KnotsCount=2 Degree=2 IsPeriodic=0
    g247: GeomPoint X=371.567 Y=-80.8644 Z=0
    g248: GeomPoint X=375.073 Y=-78.7896 Z=0
    g249: Circle CenterX=321.579 CenterY=-53.4075 CenterZ=0 NormalX=0 NormalY=0 NormalZ=1 AngleXU=0 Radius=1
    g250: Circle CenterX=318.073 CenterY=-51.4823 CenterZ=0 NormalX=0 NormalY=0 NormalZ=1 AngleXU=0 Radius=1
    g251: Circle CenterX=318.073 CenterY=-47.4805 CenterZ=0 NormalX=0 NormalY=0 NormalZ=1 AngleXU=0 Radius=1
    g252: BSplineCurve PolesCount=3 KnotsCount=2 Degree=2 IsPeriodic=0
    g253: GeomPoint X=321.579 Y=-53.4075 Z=0
    g254: GeomPoint X=318.073 Y=-47.4805 Z=0
    g255: LineSegment StartX=371.567 StartY=-80.8644 StartZ=0 EndX=321.579 EndY=-53.4075 EndZ=0
    g256: Circle CenterX=321.579 CenterY=-67.3492 CenterZ=0 NormalX=0 NormalY=0 NormalZ=1 AngleXU=0 Radius=1
    g257: Circle CenterX=318.073 CenterY=-65.424 CenterZ=0 NormalX=0 NormalY=0 NormalZ=1 AngleXU=0 Radius=1
    g258: Circle CenterX=318.073 CenterY=-69.424 CenterZ=0 NormalX=0 NormalY=0 NormalZ=1 AngleXU=0 Radius=1
    g259: BSplineCurve PolesCount=3 KnotsCount=2 Degree=2 IsPeriodic=0
    g260: GeomPoint X=321.579 Y=-67.3492 Z=0
    g261: GeomPoint X=318.073 Y=-69.424 Z=0
    g262: Circle CenterX=362.567 CenterY=-89.8542 CenterZ=0 NormalX=0 NormalY=0 NormalZ=1 AngleXU=0 Radius=1
    g263: Circle CenterX=366.073 CenterY=-91.7794 CenterZ=0 NormalX=0 NormalY=0 NormalZ=1 AngleXU=0 Radius=1
    g264: Circle CenterX=362.073 CenterY=-91.7794 CenterZ=0 NormalX=0 NormalY=0 NormalZ=1 AngleXU=0 Radius=1
    g265: BSplineCurve PolesCount=3 KnotsCount=2 Degree=2 IsPeriodic=0
    g266: GeomPoint X=362.567 Y=-89.8542 Z=0
    g267: GeomPoint X=362.073 Y=-91.7794 Z=0
    g268: Circle CenterX=322.073 CenterY=-91.7794 CenterZ=0 NormalX=0 NormalY=0 NormalZ=1 AngleXU=0 Radius=1
    g269: Circle CenterX=318.073 CenterY=-91.7794 CenterZ=0 NormalX=0 NormalY=0 NormalZ=1 AngleXU=0 Radius=1
    g270: Circle CenterX=318.073 CenterY=-87.7794 CenterZ=0 NormalX=0 NormalY=0 NormalZ=1 AngleXU=0 Radius=1
    g271: BSplineCurve PolesCount=3 KnotsCount=2 Degree=2 IsPeriodic=0
    g272: GeomPoint X=322.073 Y=-91.7794 Z=0
    g273: GeomPoint X=318.073 Y=-87.7794 Z=0
    g274: LineSegment StartX=362.567 StartY=-89.8542 StartZ=0 EndX=321.579 EndY=-67.3492 EndZ=0
    g275: LineSegment StartX=318.073 StartY=-69.424 StartZ=0 EndX=318.073 EndY=-87.7794 EndZ=0
    g276: LineSegment StartX=322.073 StartY=-91.7794 StartZ=0 EndX=362.073 EndY=-91.7794 EndZ=0
    g277: Circle CenterX=2.07281 CenterY=124.221 CenterZ=0 NormalX=0 NormalY=0 NormalZ=1 AngleXU=0 Radius=1
    g278: Circle CenterX=1.57905 CenterY=122.295 CenterZ=0 NormalX=0 NormalY=0 NormalZ=1 AngleXU=0 Radius=1
    g279: BSplineCurve PolesCount=3 KnotsCount=2 Degree=2 IsPeriodic=0
    g280: GeomPoint X=2.07281 Y=124.221 Z=0
    g281: GeomPoint X=1.57905 Y=122.295 Z=0
    g282: Circle CenterX=42.0728 CenterY=124.221 CenterZ=0 NormalX=0 NormalY=0 NormalZ=1 AngleXU=0 Radius=1
    g283: Circle CenterX=46.0728 CenterY=124.221 CenterZ=0 NormalX=0 NormalY=0 NormalZ=1 AngleXU=0 Radius=1
    g284: Circle CenterX=46.0728 CenterY=120.221 CenterZ=0 NormalX=0 NormalY=0 NormalZ=1 AngleXU=0 Radius=1
    g285: BSplineCurve PolesCount=3 KnotsCount=2 Degree=2 IsPeriodic=0
    g286: GeomPoint X=42.0728 Y=124.221 Z=0
    g287: GeomPoint X=46.0728 Y=120.221 Z=0
    g288: Circle CenterX=46.0728 CenterY=109.865 CenterZ=0 NormalX=0 NormalY=0 NormalZ=1 AngleXU=0 Radius=1
    g289: Circle CenterX=46.0728 CenterY=105.865 CenterZ=0 NormalX=0 NormalY=0 NormalZ=1 AngleXU=0 Radius=1
    g290: Circle CenterX=42.0728 CenterY=105.865 CenterZ=0 NormalX=0 NormalY=0 NormalZ=1 AngleXU=0 Radius=1
    g291: BSplineCurve PolesCount=3 KnotsCount=2 Degree=2 IsPeriodic=0
    g292: GeomPoint X=46.0728 Y=109.865 Z=0
    g293: GeomPoint X=42.0728 Y=105.865 Z=0
    g294: Circle CenterX=35.5028 CenterY=105.865 CenterZ=0 NormalX=0 NormalY=0 NormalZ=1 AngleXU=0 Radius=1
    g295: Circle CenterX=31.5028 CenterY=105.865 CenterZ=0 NormalX=0 NormalY=0 NormalZ=1 AngleXU=0 Radius=1
    g296: Circle CenterX=27.9965 CenterY=107.79 CenterZ=0 NormalX=0 NormalY=0 NormalZ=1 AngleXU=0 Radius=1
    g297: BSplineCurve PolesCount=3 KnotsCount=2 Degree=2 IsPeriodic=0
    g298: GeomPoint X=35.5028 Y=105.865 Z=0
    g299: GeomPoint X=27.9965 Y=107.79 Z=0
    g300: LineSegment StartX=2.07281 StartY=124.221 StartZ=0 EndX=42.0728 EndY=124.221 EndZ=0
    g301: LineSegment StartX=46.0728 StartY=120.221 StartZ=0 EndX=46.0728 EndY=109.865 EndZ=0
    g302: LineSegment StartX=42.0728 StartY=105.865 StartZ=0 EndX=35.5028 EndY=105.865 EndZ=0
    g303: LineSegment StartX=27.9965 StartY=107.79 StartZ=0 EndX=1.57905 EndY=122.295 EndZ=0
    g304: Circle CenterX=42.5666 CenterY=-67.3492 CenterZ=0 NormalX=0 NormalY=0 NormalZ=1 AngleXU=0 Radius=1
    g305: Circle CenterX=46.0728 CenterY=-65.424 CenterZ=0 NormalX=0 NormalY=0 NormalZ=1 AngleXU=0 Radius=1
    g306: Circle CenterX=46.0728 CenterY=-69.424 CenterZ=0 NormalX=0 NormalY=0 NormalZ=1 AngleXU=0 Radius=1
    g307: BSplineCurve PolesCount=3 KnotsCount=2 Degree=2 IsPeriodic=0
    g308: GeomPoint X=42.5666 Y=-67.3492 Z=0
    g309: GeomPoint X=46.0728 Y=-69.424 Z=0
    g310: Circle CenterX=46.0728 CenterY=-87.7794 CenterZ=0 NormalX=0 NormalY=0 NormalZ=1 AngleXU=0 Radius=1
    g311: Circle CenterX=46.0728 CenterY=-91.7794 CenterZ=0 NormalX=0 NormalY=0 NormalZ=1 AngleXU=0 Radius=1
    g312: Circle CenterX=42.0728 CenterY=-91.7794 CenterZ=0 NormalX=0 NormalY=0 NormalZ=1 AngleXU=0 Radius=1
    g313: BSplineCurve PolesCount=3 KnotsCount=2 Degree=2 IsPeriodic=0
    g314: GeomPoint X=46.0728 Y=-87.7794 Z=0
    g315: GeomPoint X=42.0728 Y=-91.7794 Z=0
    g316: Circle CenterX=2.07281 CenterY=-91.7794 CenterZ=0 NormalX=0 NormalY=0 NormalZ=1 AngleXU=0 Radius=1
    g317: Circle CenterX=-1.92719 CenterY=-91.7794 CenterZ=0 NormalX=0 NormalY=0 NormalZ=1 AngleXU=0 Radius=1
    g318: Circle CenterX=1.57905 CenterY=-89.8542 CenterZ=0 NormalX=0 NormalY=0 NormalZ=1 AngleXU=0 Radius=1
    g319: BSplineCurve PolesCount=3 KnotsCount=2 Degree=2 IsPeriodic=0
    g320: GeomPoint X=2.07281 Y=-91.7794 Z=0
    g321: GeomPoint X=1.57905 Y=-89.8542 Z=0
    g322: LineSegment StartX=2.07281 StartY=-91.7794 StartZ=0 EndX=42.0728 EndY=-91.7794 EndZ=0
    g323: LineSegment StartX=46.0728 StartY=-87.7794 StartZ=0 EndX=46.0728 EndY=-69.424 EndZ=0
    g324: LineSegment StartX=42.5666 StartY=-67.3492 StartZ=0 EndX=1.57905 EndY=-89.8542 EndZ=0
    g325: Circle CenterX=322.073 CenterY=76.4095 CenterZ=0 NormalX=0 NormalY=0 NormalZ=1 AngleXU=0 Radius=4
    g326: BSplineCurve PolesCount=3 KnotsCount=2 Degree=2 IsPeriodic=0
    g327: GeomPoint X=318.073 Y=72.4095 Z=0
    g328: GeomPoint X=322.073 Y=76.4095 Z=0
    g329: Circle CenterX=375.073 CenterY=72.4095 CenterZ=0 NormalX=0 NormalY=0 NormalZ=1 AngleXU=0 Radius=1
    g330: Circle CenterX=375.073 CenterY=76.4095 CenterZ=0 NormalX=0 NormalY=0 NormalZ=1 AngleXU=0 Radius=1
    g331: Circle CenterX=371.073 CenterY=76.4095 CenterZ=0 NormalX=0 NormalY=0 NormalZ=1 AngleXU=0 Radius=1
    g332: BSplineCurve PolesCount=3 KnotsCount=2 Degree=2 IsPeriodic=0
    g333: GeomPoint X=375.073 Y=72.4095 Z=0
    g334: GeomPoint X=371.073 Y=76.4095 Z=0
    g335: LineSegment StartX=322.073 StartY=76.4095 StartZ=0 EndX=371.073 EndY=76.4095 EndZ=0
    g336: LineSegment StartX=318.073 StartY=72.4095 StartZ=0 EndX=318.073 EndY=-47.4805 EndZ=0
    g337: LineSegment StartX=375.073 StartY=72.4095 StartZ=0 EndX=375.073 EndY=-78.7896 EndZ=0
    g338: ArcOfCircle CenterX=-26.9272 CenterY=22.1087 CenterZ=0 NormalX=0 NormalY=0 NormalZ=1 AngleXU=0 Radius=4 StartAngle=5e-16 EndAngle=3.14159
    g339: LineSegment StartX=-22.9272 StartY=22.1087 StartZ=0 EndX=-18.9272 EndY=-83.7794 EndZ=0
    g340: LineSegment StartX=-34.9272 StartY=-83.7794 StartZ=0 EndX=-30.9272 EndY=22.1087 EndZ=0
    g341: ArcOfCircle CenterX=391.073 CenterY=22.1087 CenterZ=0 NormalX=0 NormalY=0 NormalZ=1 AngleXU=0 Radius=4 StartAngle=0 EndAngle=3.14159
    g342: LineSegment StartX=387.073 StartY=22.1087 StartZ=0 EndX=383.073 EndY=-83.7794 EndZ=0
    g343: LineSegment StartX=395.073 StartY=22.1087 StartZ=0 EndX=399.073 EndY=-83.7794 EndZ=0
    g344: Circle CenterX=-10.9272 CenterY=-78.7794 CenterZ=0 NormalX=0 NormalY=0 NormalZ=1 AngleXU=0 Radius=1
    g345: Circle CenterX=-10.9272 CenterY=-82.7794 CenterZ=0 NormalX=0 NormalY=0 NormalZ=1 AngleXU=0 Radius=1
    g346: Circle CenterX=-7.42095 CenterY=-80.8542 CenterZ=0 NormalX=0 NormalY=0 NormalZ=1 AngleXU=0 Radius=1
    g347: BSplineCurve PolesCount=3 KnotsCount=2 Degree=2 IsPeriodic=0
    g348: GeomPoint X=-10.9272 Y=-78.7794 Z=0
    g349: GeomPoint X=-7.42095 Y=-80.8542 Z=0
    g350: Circle CenterX=42.5666 CenterY=-53.4075 CenterZ=0 NormalX=0 NormalY=0 NormalZ=1 AngleXU=0 Radius=1
    g351: Circle CenterX=46.0728 CenterY=-51.4823 CenterZ=0 NormalX=0 NormalY=0 NormalZ=1 AngleXU=0 Radius=1
    g352: Circle CenterX=46.0728 CenterY=-47.4823 CenterZ=0 NormalX=0 NormalY=0 NormalZ=1 AngleXU=0 Radius=1
    g353: BSplineCurve PolesCount=3 KnotsCount=2 Degree=2 IsPeriodic=0
    g354: GeomPoint X=42.5666 Y=-53.4075 Z=0
    g355: GeomPoint X=46.0728 Y=-47.4823 Z=0
    g356: Circle CenterX=46.0728 CenterY=72.4095 CenterZ=0 NormalX=0 NormalY=0 NormalZ=1 AngleXU=0 Radius=1
    g357: Circle CenterX=46.0728 CenterY=76.4095 CenterZ=0 NormalX=0 NormalY=0 NormalZ=1 AngleXU=0 Radius=1
    g358: Circle CenterX=42.0728 CenterY=76.4095 CenterZ=0 NormalX=0 NormalY=0 NormalZ=1 AngleXU=0 Radius=1
    g359: BSplineCurve PolesCount=3 KnotsCount=2 Degree=2 IsPeriodic=0
    g360: GeomPoint X=46.0728 Y=72.4095 Z=0
    g361: GeomPoint X=42.0728 Y=76.4095 Z=0
    g362: Circle CenterX=-6.92718 CenterY=76.4095 CenterZ=0 NormalX=0 NormalY=0 NormalZ=1 AngleXU=0 Radius=1
    g363: Circle CenterX=-10.9272 CenterY=76.4095 CenterZ=0 NormalX=0 NormalY=0 NormalZ=1 AngleXU=0 Radius=1
    g364: Circle CenterX=-10.9272 CenterY=72.4095 CenterZ=0 NormalX=0 NormalY=0 NormalZ=1 AngleXU=0 Radius=1
    g365: BSplineCurve PolesCount=3 KnotsCount=2 Degree=2 IsPeriodic=0
    g366: GeomPoint X=-6.92718 Y=76.4095 Z=0
    g367: GeomPoint X=-10.9272 Y=72.4095 Z=0
    g368: LineSegment StartX=-10.9272 StartY=72.4095 StartZ=0 EndX=-10.9272 EndY=-78.7794 EndZ=0
    g369: LineSegment StartX=-7.42095 StartY=-80.8542 StartZ=0 EndX=42.5666 EndY=-53.4075 EndZ=0
    g370: LineSegment StartX=46.0728 StartY=-47.4823 StartZ=0 EndX=46.0728 EndY=72.4095 EndZ=0
    g371: LineSegment StartX=42.0728 StartY=76.4095 StartZ=0 EndX=-6.92719 EndY=76.4095 EndZ=0
    g372: LineSegment StartX=232.072 StartY=136.221 StartZ=0 EndX=232.072 EndY=-117.815 EndZ=0
    g373: LineSegment StartX=132.072 StartY=136.221 StartZ=0 EndX=132.072 EndY=-121.309 EndZ=0
    g374: LineSegment StartX=245.072 StartY=136.221 StartZ=0 EndX=245.072 EndY=-116.499 EndZ=0
    g375: LineSegment StartX=119.072 StartY=136.221 StartZ=0 EndX=119.072 EndY=-116.228 EndZ=0
    g376: LineSegment StartX=-42.9272 StartY=136.221 StartZ=0 EndX=407.073 EndY=136.221 EndZ=0
    g377: LineSegment StartX=232.072 StartY=136.221 StartZ=0 EndX=220.072 EndY=136.221 EndZ=0
    g378: LineSegment StartX=232.072 StartY=136.221 StartZ=0 EndX=232.072 EndY=124.221 EndZ=0
  constraints (630):
    c: Vertical(g0)
    c: Vertical(g1)
    c: Block(g1)
    c: Block(g0)
    c: Weight(g4) = 1
    c: Equal(g4,g5)
    c: Equal(g4,g6)
    c: InternalAlignment(g4,g7)
    c: InternalAlignment(g5,g7)
    c: InternalAlignment(g6,g7)
    c: InternalAlignment(g8,g7)
    c: InternalAlignment(g9,g7)
    c: Weight(g10) = 1
    c: Equal(g10,g11)
    c: Equal(g10,g12)
    c: InternalAlignment(g10,g13)
    c: InternalAlignment(g11,g13)
    c: InternalAlignment(g12,g13)
    c: InternalAlignment(g14,g13)
    c: InternalAlignment(g15,g13)
    c: Block(g13)
    c: Block(g7)
    c: Weight(g16) = 1
    c: Equal(g16,g17)
    c: Equal(g16,g18)
    c: InternalAlignment(g16,g19)
    c: InternalAlignment(g17,g19)
    c: InternalAlignment(g18,g19)
    c: InternalAlignment(g20,g19)
    c: InternalAlignment(g21,g19)
    c: Weight(g22) = 1
    c: Equal(g22,g23)
    c: Equal(g22,g24)
    c: InternalAlignment(g22,g25)
    c: InternalAlignment(g23,g25)
    c: InternalAlignment(g24,g25)
    c: InternalAlignment(g26,g25)
    c: InternalAlignment(g27,g25)
    c: Block(g25)
    c: Block(g19)
    c: Weight(g28) = 1
    c: Equal(g28,g29)
    c: Equal(g28,g30)
    c: InternalAlignment(g28,g31)
    c: InternalAlignment(g29,g31)
    c: InternalAlignment(g30,g31)
    c: InternalAlignment(g32,g31)
    c: InternalAlignment(g33,g31)
    c: Weight(g34) = 1
    c: Equal(g34,g35)
    c: Equal(g34,g36)
    c: InternalAlignment(g34,g37)
    c: InternalAlignment(g35,g37)
    c: InternalAlignment(g36,g37)
    c: InternalAlignment(g38,g37)
    c: InternalAlignment(g39,g37)
    c: Block(g31)
    c: Block(g37)
    c: Coincident(g40,g1)
    c: Coincident(g40,g0)
    c: Horizontal(g40)
    c: Distance(g40) = 450
    c: Weight(g41) = 1
    c: Equal(g41,g42)
    c: Equal(g41,g43)
    c: InternalAlignment(g41,g44)
    c: InternalAlignment(g42,g44)
    c: InternalAlignment(g43,g44)
    c: InternalAlignment(g45,g44)
    c: InternalAlignment(g46,g44)
    c: Block(g44)
    c: Weight(g47) = 1
    c: Equal(g47,g48)
    c: Equal(g47,g49)
    c: InternalAlignment(g47,g50)
    c: InternalAlignment(g48,g50)
    c: InternalAlignment(g49,g50)
    c: InternalAlignment(g51,g50)
    c: InternalAlignment(g52,g50)
    c: Block(g50)
    c: Weight(g53) = 1
    c: Equal(g53,g54)
    c: Equal(g53,g55)
    c: InternalAlignment(g53,g56)
    c: InternalAlignment(g54,g56)
    c: InternalAlignment(g55,g56)
    c: InternalAlignment(g57,g56)
    c: InternalAlignment(g58,g56)
    c: Block(g56)
    c: Weight(g59) = 1
    c: Equal(g59,g60)
    c: Equal(g59,g61)
    c: InternalAlignment(g59,g62)
    c: InternalAlignment(g60,g62)
    c: InternalAlignment(g61,g62)
    c: InternalAlignment(g63,g62)
    c: InternalAlignment(g64,g62)
    c: Block(g62)
    c: Weight(g65) = 1
    c: Equal(g65,g66)
    c: Equal(g65,g67)
    c: InternalAlignment(g65,g68)
    c: InternalAlignment(g66,g68)
    c: InternalAlignment(g67,g68)
    c: InternalAlignment(g69,g68)
    c: InternalAlignment(g70,g68)
    c: Weight(g71) = 1
    c: Equal(g71,g72)
    c: Equal(g71,g73)
    c: InternalAlignment(g71,g74)
    c: InternalAlignment(g72,g74)
    c: InternalAlignment(g73,g74)
    c: InternalAlignment(g75,g74)
    c: InternalAlignment(g76,g74)
    c: Block(g68)
    c: Block(g74)
    c: Coincident(g77,g68)
    c: Coincident(g77,g74)
    c: Vertical(g77)
    c: Coincident(g78,g68)
    c: Coincident(g78,g50)
    c: Coincident(g79,g50)
    c: Coincident(g79,g74)
    c: Weight(g80) = 1
    c: Equal(g80,g81)
    c: Equal(g80,g82)
    c: InternalAlignment(g80,g83)
    c: InternalAlignment(g81,g83)
    c: InternalAlignment(g82,g83)
    c: InternalAlignment(g84,g83)
    c: InternalAlignment(g85,g83)
    c: Weight(g86) = 1
    c: Equal(g86,g87)
    c: Equal(g86,g88)
    c: InternalAlignment(g86,g89)
    c: InternalAlignment(g87,g89)
    c: InternalAlignment(g88,g89)
    c: InternalAlignment(g90,g89)
    c: InternalAlignment(g91,g89)
    c: Block(g83)
    c: Block(g89)
    c: Coincident(g92,g83)
    c: Coincident(g92,g89)
    c: Vertical(g92)
    c: Coincident(g93,g83)
    c: Coincident(g93,g44)
    c: Coincident(g94,g44)
    c: Coincident(g94,g89)
    c: Weight(g95) = 1
    c: Equal(g95,g96)
    c: Equal(g95,g97)
    c: InternalAlignment(g95,g98)
    c: InternalAlignment(g96,g98)
    c: InternalAlignment(g97,g98)
    c: InternalAlignment(g99,g98)
    c: InternalAlignment(g100,g98)
    c: Weight(g101) = 1
    c: Equal(g101,g102)
    c: Equal(g101,g103)
    c: InternalAlignment(g101,g104)
    c: InternalAlignment(g102,g104)
    c: InternalAlignment(g103,g104)
    c: InternalAlignment(g105,g104)
    c: InternalAlignment(g106,g104)
    c: Block(g98)
    c: Block(g104)
    c: Coincident(g107,g98)
    c: Coincident(g107,g104)
    c: Vertical(g107)
    c: Coincident(g108,g104)
    c: Coincident(g108,g62)
    c: Coincident(g109,g62)
    c: Coincident(g109,g98)
    c: Weight(g110) = 1
    c: Equal(g110,g111)
    c: Equal(g110,g112)
    c: InternalAlignment(g110,g113)
    c: InternalAlignment(g111,g113)
    c: InternalAlignment(g112,g113)
    c: InternalAlignment(g114,g113)
    c: InternalAlignment(g115,g113)
    c: Weight(g116) = 1
    c: Equal(g116,g117)
    c: Equal(g116,g118)
    c: InternalAlignment(g116,g119)
    c: InternalAlignment(g117,g119)
    c: InternalAlignment(g118,g119)
    c: InternalAlignment(g120,g119)
    c: InternalAlignment(g121,g119)
    c: Block(g113)
    c: Block(g119)
    c: Coincident(g122,g113)
    c: Coincident(g122,g119)
    c: Vertical(g122)
    c: Coincident(g123,g119)
    c: Coincident(g123,g56)
    c: Coincident(g124,g56)
    c: Coincident(g124,g113)
    c: Weight(g125) = 1
    c: Equal(g125,g126)
    c: Equal(g125,g127)
    c: InternalAlignment(g125,g128)
    c: InternalAlignment(g126,g128)
    c: InternalAlignment(g127,g128)
    c: InternalAlignment(g129,g128)
    c: InternalAlignment(g130,g128)
    c: Weight(g131) = 1
    c: Equal(g131,g132)
    c: Equal(g131,g133)
    c: InternalAlignment(g131,g134)
    c: InternalAlignment(g132,g134)
    c: InternalAlignment(g133,g134)
    c: InternalAlignment(g135,g134)
    c: InternalAlignment(g136,g134)
    c: Weight(g137) = 1
    c: Equal(g137,g138)
    c: Equal(g137,g139)
    c: InternalAlignment(g137,g140)
    c: InternalAlignment(g138,g140)
    c: InternalAlignment(g139,g140)
    c: InternalAlignment(g141,g140)
    c: InternalAlignment(g142,g140)
    c: Weight(g143) = 1
    c: Equal(g143,g144)
    c: Equal(g143,g145)
    c: InternalAlignment(g143,g146)
    c: InternalAlignment(g144,g146)
    c: InternalAlignment(g145,g146)
    c: InternalAlignment(g147,g146)
    c: InternalAlignment(g148,g146)
    c: Block(g146)
    c: Block(g140)
    c: Block(g134)
    c: Block(g128)
    c: Coincident(g149,g25)
    c: Coincident(g149,g146)
    c: Coincident(g150,g146)
    c: Coincident(g150,g140)
    c: Horizontal(g150)
    c: Coincident(g151,g140)
    c: Coincident(g151,g25)
    c: Vertical(g151)
    c: Coincident(g152,g19)
    c: Coincident(g152,g134)
    c: Vertical(g152)
    c: Coincident(g153,g134)
    c: Coincident(g153,g128)
    c: Horizontal(g153)
    c: Coincident(g154,g128)
    c: Coincident(g154,g19)
    c: Weight(g155) = 1
    c: Equal(g155,g156)
    c: Equal(g155,g157)
    c: InternalAlignment(g155,g158)
    c: InternalAlignment(g156,g158)
    c: InternalAlignment(g157,g158)
    c: InternalAlignment(g159,g158)
    c: InternalAlignment(g160,g158)
    c: Weight(g161) = 1
    c: Equal(g161,g162)
    c: Equal(g161,g163)
    c: InternalAlignment(g161,g164)
    c: InternalAlignment(g162,g164)
    c: InternalAlignment(g163,g164)
    c: InternalAlignment(g165,g164)
    c: InternalAlignment(g166,g164)
    c: Weight(g167) = 1
    c: Equal(g167,g168)
    c: Equal(g167,g169)
    c: InternalAlignment(g167,g170)
    c: InternalAlignment(g168,g170)
    c: InternalAlignment(g169,g170)
    c: InternalAlignment(g171,g170)
    c: InternalAlignment(g172,g170)
    c: Weight(g173) = 1
    c: Equal(g173,g174)
    c: Equal(g173,g175)
    c: InternalAlignment(g173,g176)
    c: InternalAlignment(g174,g176)
    c: InternalAlignment(g175,g176)
    c: InternalAlignment(g177,g176)
    c: InternalAlignment(g178,g176)
    c: Block(g176)
    c: Block(g170)
    c: Block(g164)
    c: Block(g158)
    c: Coincident(g179,g176)
    c: Coincident(g179,g170)
    c: Horizontal(g179)
    c: Coincident(g180,g170)
    c: Coincident(g180,g7)
    c: Vertical(g180)
    c: Coincident(g181,g13)
    c: Coincident(g181,g164)
    c: Vertical(g181)
    c: Coincident(g182,g164)
    c: Coincident(g182,g158)
    c: Horizontal(g182)
    c: Coincident(g183,g158)
    c: Coincident(g183,g13)
    c: Coincident(g184,g7)
    c: Weight(g185) = 1
    c: Equal(g185,g186)
    c: Equal(g185,g187)
    c: InternalAlignment(g185,g188)
    c: InternalAlignment(g186,g188)
    c: InternalAlignment(g187,g188)
    c: InternalAlignment(g189,g188)
    c: InternalAlignment(g190,g188)
    c: Weight(g191) = 1
    c: Equal(g191,g192)
    c: Equal(g191,g193)
    c: InternalAlignment(g191,g194)
    c: InternalAlignment(g192,g194)
    c: InternalAlignment(g193,g194)
    c: InternalAlignment(g195,g194)
    c: InternalAlignment(g196,g194)
    c: Block(g194)
    c: Block(g188)
    c: Coincident(g197,g194)
    c: Coincident(g197,g31)
    c: Coincident(g198,g31)
    c: Coincident(g198,g188)
    c: Coincident(g199,g188)
    c: Coincident(g199,g194)
    c: Vertical(g199)
    c: Weight(g200) = 1
    c: Equal(g200,g201)
    c: Equal(g200,g202)
    c: InternalAlignment(g200,g203)
    c: InternalAlignment(g201,g203)
    c: InternalAlignment(g202,g203)
    c: InternalAlignment(g204,g203)
    c: InternalAlignment(g205,g203)
    c: Weight(g206) = 1
    c: Equal(g206,g207)
    c: Equal(g206,g208)
    c: InternalAlignment(g206,g209)
    c: InternalAlignment(g207,g209)
    c: InternalAlignment(g208,g209)
    c: InternalAlignment(g210,g209)
    c: InternalAlignment(g211,g209)
    c: Block(g209)
    c: Block(g203)
    c: Coincident(g212,g203)
    c: Coincident(g212,g37)
    c: Coincident(g213,g37)
    c: Coincident(g213,g209)
    c: Coincident(g214,g209)
    c: Coincident(g214,g203)
    c: Vertical(g214)
    c: Horizontal(g215)
    c: Block(g215)
    c: Vertical(g216)
    c: Block(g216)
    c: Block(g217)
    c: Weight(g218) = 1
    c: Equal(g218,g219)
    c: Equal(g218,g220)
    c: InternalAlignment(g218,g221)
    c: InternalAlignment(g219,g221)
    c: InternalAlignment(g220,g221)
    c: InternalAlignment(g222,g221)
    c: InternalAlignment(g223,g221)
    c: Weight(g224) = 1
    c: Equal(g224,g225)
    c: Equal(g224,g226)
    c: InternalAlignment(g224,g227)
    c: InternalAlignment(g225,g227)
    c: InternalAlignment(g226,g227)
    c: InternalAlignment(g228,g227)
    c: InternalAlignment(g229,g227)
    c: Weight(g230) = 1
    c: Equal(g230,g231)
    c: Equal(g230,g232)
    c: InternalAlignment(g230,g233)
    c: InternalAlignment(g231,g233)
    c: InternalAlignment(g232,g233)
    c: InternalAlignment(g234,g233)
    c: InternalAlignment(g235,g233)
    c: Weight(g236) = 1
    c: Equal(g236,g237)
    c: Equal(g236,g238)
    c: InternalAlignment(g236,g239)
    c: InternalAlignment(g237,g239)
    c: InternalAlignment(g238,g239)
    c: InternalAlignment(g240,g239)
    c: InternalAlignment(g241,g239)
    c: Block(g221)
    c: Block(g227)
    c: Block(g233)
    c: Block(g239)
    c: Coincident(g242,g227)
    c: Coincident(g242,g221)
    c: Horizontal(g242)
    c: Block(g184)
    c: Weight(g243) = 1
    c: Equal(g243,g244)
    c: Equal(g243,g245)
    c: InternalAlignment(g243,g246)
    c: InternalAlignment(g244,g246)
    c: InternalAlignment(g245,g246)
    c: InternalAlignment(g247,g246)
    c: InternalAlignment(g248,g246)
    c: Weight(g249) = 1
    c: Equal(g249,g250)
    c: Equal(g249,g251)
    c: InternalAlignment(g249,g252)
    c: InternalAlignment(g250,g252)
    c: InternalAlignment(g251,g252)
    c: InternalAlignment(g253,g252)
    c: InternalAlignment(g254,g252)
    c: Block(g246)
    c: Block(g252)
    c: Coincident(g255,g246)
    c: Coincident(g255,g252)
    c: Weight(g256) = 1
    c: Equal(g256,g257)
    c: Equal(g256,g258)
    c: InternalAlignment(g256,g259)
    c: InternalAlignment(g257,g259)
    c: InternalAlignment(g258,g259)
    c: InternalAlignment(g260,g259)
    c: InternalAlignment(g261,g259)
    c: Weight(g262) = 1
    c: Equal(g262,g263)
    c: Equal(g262,g264)
    c: InternalAlignment(g262,g265)
    c: InternalAlignment(g263,g265)
    c: InternalAlignment(g264,g265)
    c: InternalAlignment(g266,g265)
    c: InternalAlignment(g267,g265)
    c: Weight(g268) = 1
    c: Equal(g268,g269)
    c: Equal(g268,g270)
    c: InternalAlignment(g268,g271)
    c: InternalAlignment(g269,g271)
    c: InternalAlignment(g270,g271)
    c: InternalAlignment(g272,g271)
    c: InternalAlignment(g273,g271)
    c: Block(g271)
    c: Block(g265)
    c: Block(g259)
    c: Coincident(g274,g265)
    c: Coincident(g274,g259)
    c: Coincident(g275,g259)
    c: Coincident(g275,g271)
    c: Vertical(g275)
    c: Coincident(g276,g271)
    c: Coincident(g276,g265)
    c: Horizontal(g276)
    c: Weight(g277) = 1
    c: Equal(g277,g278)
    c: InternalAlignment(g277,g279)
    c: InternalAlignment(g278,g279)
    c: InternalAlignment(g280,g279)
    c: InternalAlignment(g281,g279)
    c: Weight(g282) = 1
    c: InternalAlignment(g283,g285)
    c: InternalAlignment(g284,g285)
    c: InternalAlignment(g286,g285)
    c: InternalAlignment(g287,g285)
    c: Weight(g288) = 1
    c: Equal(g288,g289)
    c: Equal(g288,g290)
    c: InternalAlignment(g288,g291)
    c: InternalAlignment(g289,g291)
    c: InternalAlignment(g290,g291)
    c: InternalAlignment(g292,g291)
    c: InternalAlignment(g293,g291)
    c: Equal(g294,g295)
    c: Equal(g294,g296)
    c: InternalAlignment(g294,g297)
    c: InternalAlignment(g295,g297)
    c: InternalAlignment(g296,g297)
    c: InternalAlignment(g298,g297)
    c: InternalAlignment(g299,g297)
    c: Block(g285)
    c: Block(g291)
    c: Block(g297)
    c: Block(g279)
    c: Coincident(g300,g279)
    c: Coincident(g300,g285)
    c: Horizontal(g300)
    c: Coincident(g301,g285)
    c: Coincident(g301,g291)
    c: Vertical(g301)
    c: Coincident(g302,g291)
    c: Coincident(g302,g297)
    c: Horizontal(g302)
    c: Coincident(g303,g297)
    c: Coincident(g303,g279)
    c: Weight(g304) = 1
    c: Equal(g304,g305)
    c: Equal(g304,g306)
    c: InternalAlignment(g304,g307)
    c: InternalAlignment(g305,g307)
    c: InternalAlignment(g306,g307)
    c: InternalAlignment(g308,g307)
    c: InternalAlignment(g309,g307)
    c: Weight(g310) = 1
    c: Equal(g310,g311)
    c: Equal(g310,g312)
    c: InternalAlignment(g310,g313)
    c: InternalAlignment(g311,g313)
    c: InternalAlignment(g312,g313)
    c: InternalAlignment(g314,g313)
    c: InternalAlignment(g315,g313)
    c: Weight(g316) = 1
    c: Equal(g316,g317)
    c: Equal(g316,g318)
    c: InternalAlignment(g316,g319)
    c: InternalAlignment(g317,g319)
    c: InternalAlignment(g318,g319)
    c: InternalAlignment(g320,g319)
    c: InternalAlignment(g321,g319)
    c: Block(g319)
    c: Block(g313)
    c: Block(g307)
    c: Coincident(g322,g319)
    c: Coincident(g322,g313)
    c: Horizontal(g322)
    c: Coincident(g323,g313)
    c: Coincident(g323,g307)
    c: Vertical(g323)
    c: Coincident(g324,g307)
    c: Coincident(g324,g319)
    c: InternalAlignment(g325,g326)
    c: InternalAlignment(g327,g326)
    c: InternalAlignment(g328,g326)
    c: Block(g326)
    c: Equal(g329,g330)
    c: Equal(g329,g331)
    c: InternalAlignment(g329,g332)
    c: InternalAlignment(g330,g332)
    c: InternalAlignment(g331,g332)
    c: InternalAlignment(g333,g332)
    c: InternalAlignment(g334,g332)
    c: Block(g332)
    c: Coincident(g335,g326)
    c: Horizontal(g335)
    c: Block(g335)
    c: Coincident(g336,g326)
    c: Coincident(g336,g252)
    c: Vertical(g336)
    c: Coincident(g337,g332)
    c: Coincident(g337,g246)
    c: Vertical(g337)
    c: Block(g338)
    c: Block(g2)
    c: Distance(g336) = 119.89
    c: Coincident(g339,g338)
    c: Coincident(g339,g2)
    c: Coincident(g340,g2)
    c: Coincident(g340,g338)
    c: Block(g3)
    c: Block(g341)
    c: Coincident(g342,g341)
    c: Coincident(g342,g3)
    c: Coincident(g343,g341)
    c: Coincident(g343,g3)
    c: Block(g343)
    c: Block(g342)
    c: Weight(g344) = 1
    c: Equal(g344,g345)
    c: Equal(g344,g346)
    c: InternalAlignment(g344,g347)
    c: InternalAlignment(g345,g347)
    c: InternalAlignment(g346,g347)
    c: InternalAlignment(g348,g347)
    c: InternalAlignment(g349,g347)
    c: Weight(g350) = 1
    c: Equal(g350,g351)
    c: Equal(g350,g352)
    c: InternalAlignment(g350,g353)
    c: InternalAlignment(g351,g353)
    c: InternalAlignment(g352,g353)
    c: InternalAlignment(g354,g353)
    c: InternalAlignment(g355,g353)
    c: Weight(g356) = 1
    c: Equal(g356,g357)
    c: Equal(g356,g358)
    c: InternalAlignment(g356,g359)
    c: InternalAlignment(g357,g359)
    c: InternalAlignment(g358,g359)
    c: InternalAlignment(g360,g359)
    c: InternalAlignment(g361,g359)
    c: Weight(g362) = 1
    c: Equal(g362,g363)
    c: Equal(g362,g364)
    c: InternalAlignment(g362,g365)
    c: InternalAlignment(g363,g365)
    c: InternalAlignment(g364,g365)
    c: InternalAlignment(g366,g365)
    c: InternalAlignment(g367,g365)
    c: Block(g365)
    c: Block(g359)
    c: Block(g353)
    c: Block(g347)
    c: Coincident(g368,g365)
    c: Coincident(g368,g347)
    c: Vertical(g368)
    c: Coincident(g369,g347)
    c: Coincident(g369,g353)
    c: Coincident(g370,g353)
    c: Coincident(g370,g359)
    c: Vertical(g370)
    c: Coincident(g371,g359)
    c: Coincident(g371,g365)
    c: Horizontal(g371)
    c: Vertical(g372)
    c: Vertical(g373)
    c: Vertical(g374)
    c: Vertical(g375)
    c: Coincident(g376,g0)
    c: Coincident(g376,g1)
    c: Horizontal(g376)
    c: Block(g376)
    c: Distance(g376) = 450
    c: Block(g374)
    c: Block(g372)
    c: Block(g373)
    c: Block(g375)
    c: Distance(g0) = 240
    c: Horizontal(g377)
    c: Distance(g377) = 12
    c: Coincident(g377,g372)
    c: Vertical(g378)
    c: Distance(g378) = 12
    c: Coincident(g378,g372)
FEATURE [Part::Extrusion] Extrude005
  Base = -> Sketch003
  Dir = (0,0,1)
  DirMode = 2
  FaceMakerClass = Part::FaceMakerBullseye
  LengthFwd = 24
  LengthRev = 0
  Solid = true
  Symmetric = false
